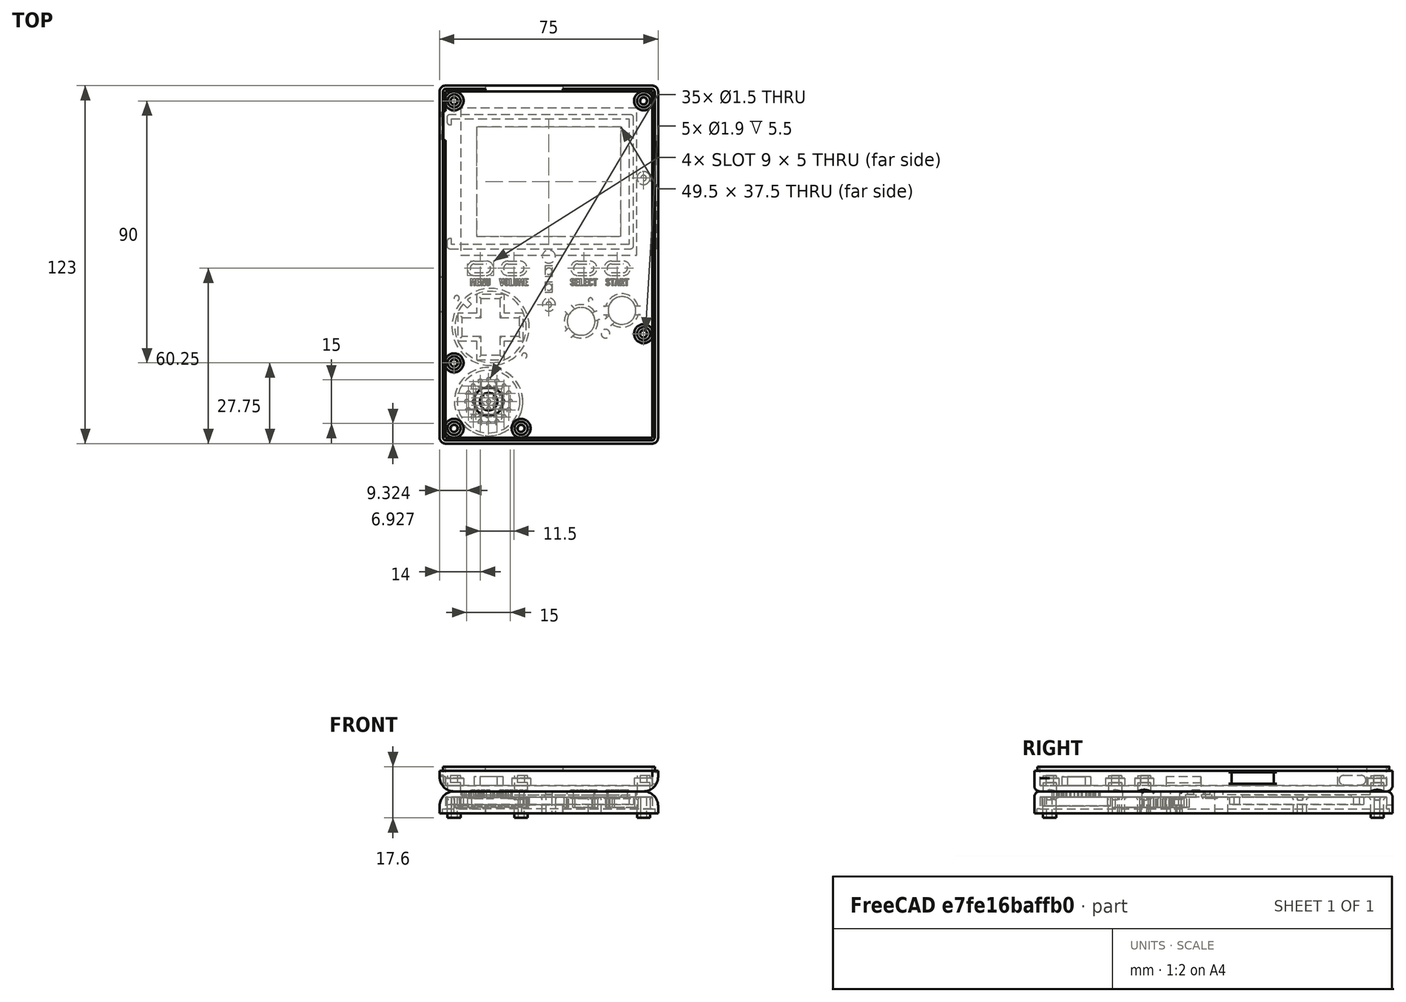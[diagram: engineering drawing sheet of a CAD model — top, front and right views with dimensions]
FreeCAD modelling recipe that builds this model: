
FCSTD DOCUMENT  (FreeCAD 1.0R39319 (Git))
Label: redroid_go
License: All rights reserved
LicenseURL: https://en.wikipedia.org/wiki/All_rights_reserved
objects: Sketcher::SketchObject×37, PartDesign::Pad×18, PartDesign::Pocket×15, PartDesign::Fillet×14, PartDesign::SubShapeBinder×6, Part::Part2DObjectPython×4, Part::Extrusion×4, PartDesign::PolarPattern×3, Measure::MeasureLength×3, PartDesign::Body×2, Spreadsheet::Sheet×1, Measure::MeasureDistance×1, App::DocumentObjectGroup×1
note: 237 computed .brp shape members not serialized (recipe doc carries the construction recipe); baked Part::Feature solids carry a one-line shape summary decoded from their .brp

FEATURE [Spreadsheet::Sheet] Spreadsheet
  cells = A1='thickness; B1=2; A2='front_height; B2=5.5; A3='pcb_height; B3=1.6; A4='back_height; B4=3.5; A5='edges_fillet; B5=2
FEATURE [Sketcher::SketchObject] Sketch021  label="skrews"
  ArcFitTolerance = 1e-06
  AttachmentOffset = pos=(0,0,-2) rot=(0,0,1;0rad)
  AttachmentSupport = -> [XY_Plane002]
  FullyConstrained = true
  MakeInternals = false
  MapMode = 5
  Placement = pos=(0,0,-2) rot=(0,0,1;0rad)
  sketch-geometry (21):
    g0: Circle CenterX=-32.525 CenterY=45 CenterZ=0 NormalX=0 NormalY=0 NormalZ=1 AngleXU=0 Radius=0.95
    g1: Circle CenterX=-32.525 CenterY=-45 CenterZ=0 NormalX=0 NormalY=0 NormalZ=1 AngleXU=0 Radius=0.95
    g2: Circle CenterX=32.525 CenterY=18.5 CenterZ=0 NormalX=0 NormalY=0 NormalZ=1 AngleXU=0 Radius=0.95
    g3: Circle CenterX=32.525 CenterY=-35 CenterZ=0 NormalX=0 NormalY=0 NormalZ=1 AngleXU=0 Radius=0.95
    g4: Circle CenterX=-32.525 CenterY=45 CenterZ=0 NormalX=0 NormalY=0 NormalZ=1 AngleXU=0 Radius=2.25
    g5: Circle CenterX=-32.525 CenterY=-45 CenterZ=0 NormalX=0 NormalY=0 NormalZ=1 AngleXU=0 Radius=2.25
    g6: Circle CenterX=32.525 CenterY=-35 CenterZ=0 NormalX=0 NormalY=0 NormalZ=1 AngleXU=0 Radius=2.25
    g7: Circle CenterX=32.525 CenterY=18.5 CenterZ=0 NormalX=0 NormalY=0 NormalZ=1 AngleXU=0 Radius=2.25
    g8: LineSegment [constr] StartX=-32.525 StartY=45 StartZ=0 EndX=-32.525 EndY=-45 EndZ=0
    g9: LineSegment [constr] StartX=32.525 StartY=18.5 StartZ=0 EndX=32.525 EndY=-35 EndZ=0
    g10: LineSegment [constr] StartX=-32.525 StartY=45 StartZ=0 EndX=-32.525 EndY=-45 EndZ=0
    g11: LineSegment [constr] StartX=-32.525 StartY=-45 StartZ=0 EndX=32.525 EndY=-45 EndZ=0
    g12: LineSegment [constr] StartX=32.525 StartY=-45 StartZ=0 EndX=32.525 EndY=45 EndZ=0
    g13: LineSegment [constr] StartX=32.525 StartY=45 StartZ=0 EndX=-32.525 EndY=45 EndZ=0
    g14: Circle CenterX=0 CenterY=-25 CenterZ=0 NormalX=0 NormalY=0 NormalZ=1 AngleXU=0 Radius=0.95
    g15: Circle CenterX=0 CenterY=-25 CenterZ=0 NormalX=0 NormalY=0 NormalZ=1 AngleXU=0 Radius=2.25
    g16: LineSegment [constr] StartX=0 StartY=-25 StartZ=0 EndX=-32.525 EndY=-25 EndZ=0
    g17: LineSegment [constr] StartX=-32.525 StartY=-25 StartZ=0 EndX=-32.525 EndY=-45 EndZ=0
    g18: LineSegment [constr] StartX=-32.525 StartY=-45 StartZ=0 EndX=0 EndY=-45 EndZ=0
    g19: LineSegment [constr] StartX=0 StartY=-45 StartZ=0 EndX=0 EndY=-25 EndZ=0
    g20: Circle CenterX=0 CenterY=-8.5 CenterZ=0 NormalX=0 NormalY=0 NormalZ=1 AngleXU=0 Radius=2.25
  constraints (51):
    c: Equal(g0,g1)
    c: Equal(g1,g3)
    c: Equal(g3,g2)
    c: Diameter(g0) = 1.9
    c: Coincident(g4,g0)
    c: Coincident(g5,g1)
    c: Coincident(g6,g3)
    c: Coincident(g7,g2)
    c: Diameter(g4) = 4.5
    c: Equal(g4,g5)
    c: Equal(g5,g6)
    c: Equal(g6,g7)
    c: Coincident(g8,g0)
    c: Coincident(g8,g1)
    c: Vertical(g8)
    c: Coincident(g9,g2)
    c: Coincident(g9,g3)
    c: Vertical(g9)
    c: DistanceX(g0,g2) = 65.05
    c: DistanceY(g2,g0) = 26.5
    c: DistanceY(g8,g8) = 90
    c: DistanceY(g9,g9) = 53.5
    c: Coincident(g10,g11)
    c: Coincident(g11,g12)
    c: Coincident(g12,g13)
    c: Coincident(g13,g10)
    c: Vertical(g12)
    c: Horizontal(g11)
    c: Horizontal(g13)
    c: Coincident(g10,g0)
    c: Coincident(g10,g1)
    c: Symmetric(g11,g0,g-1)
    c: PointOnObject(g3,g12)
    c: Equal(g1,g14)
    c: Equal(g5,g15)
    c: Coincident(g16,g17)
    c: Coincident(g17,g18)
    c: Coincident(g18,g19)
    c: Coincident(g19,g16)
    c: Horizontal(g16)
    c: Horizontal(g18)
    c: Vertical(g17)
    c: Vertical(g19)
    c: Coincident(g16,g14)
    c: Coincident(g17,g1)
    c: PointOnObject(g15,g-2)
    c: Coincident(g14,g15)
    c: DistanceY(g19,g19) = 20
    c: PointOnObject(g20,g-2)
    c: Equal(g15,g20)
    c: DistanceY(g14,g20) = 16.5
FEATURE [Sketcher::SketchObject] Sketch022  label="main"
  ArcFitTolerance = 1e-06
  AttachmentSupport = -> [XY_Plane002]
  ExternalGeometry = -> [Sketch021]
  FullyConstrained = true
  MakeInternals = false
  MapMode = 5
  expr: Constraints[171] = 111.27 - 2.54 / 2 - 103.5
  expr: Constraints[184] = 11.5 - 0.4
  expr: Constraints[281] = 7.5 + 0.165
  expr: Constraints[292] = 55 - 2.54 / 2
  expr: Constraints[299] = 105.77 - 2.54 / 2 - 103.5
  sketch-geometry (119):
    g0: LineSegment StartX=-35.5 StartY=48.25 StartZ=0 EndX=-35.5 EndY=-70.75 EndZ=0
    g1: LineSegment StartX=-35.5 StartY=-70.75 StartZ=0 EndX=35.5 EndY=-70.75 EndZ=0
    g2: LineSegment StartX=35.5 StartY=-70.75 StartZ=0 EndX=35.5 EndY=48.25 EndZ=0
    g3: LineSegment StartX=35.5 StartY=48.25 StartZ=0 EndX=-35.5 EndY=48.25 EndZ=0
    g4: Circle [constr] CenterX=-32.525 CenterY=45 CenterZ=0 NormalX=0 NormalY=0 NormalZ=1 AngleXU=0 Radius=2.25
    g5: LineSegment [constr] StartX=-32.525 StartY=45 StartZ=0 EndX=-32.525 EndY=47.25 EndZ=0
    g6: LineSegment [constr] StartX=-32.525 StartY=47.25 StartZ=0 EndX=-32.525 EndY=48.25 EndZ=0
    g7: LineSegment StartX=-24.75 StartY=36 StartZ=0 EndX=-24.75 EndY=-1.5 EndZ=0
    g8: LineSegment StartX=-24.75 StartY=-1.5 StartZ=0 EndX=24.75 EndY=-1.5 EndZ=0
    g9: LineSegment StartX=24.75 StartY=-1.5 StartZ=0 EndX=24.75 EndY=36 EndZ=0
    g10: LineSegment StartX=24.75 StartY=36 StartZ=0 EndX=-24.75 EndY=36 EndZ=0
    g11: LineSegment [constr] StartX=-32.525 StartY=45 StartZ=0 EndX=-32.525 EndY=36 EndZ=0
    g12: LineSegment [constr] StartX=-32.525 StartY=36 StartZ=0 EndX=-24.75 EndY=36 EndZ=0
    g13: LineSegment [constr] StartX=-24.75 StartY=36 StartZ=0 EndX=-24.75 EndY=45 EndZ=0
    g14: LineSegment [constr] StartX=-24.75 StartY=45 StartZ=0 EndX=-32.525 EndY=45 EndZ=0
    g15: LineSegment [constr] StartX=-24.75 StartY=36 StartZ=0 EndX=24.75 EndY=-1.5 EndZ=0
    g16: GeomPoint [constr] X=0 Y=17.25 Z=0
    g17: ArcOfCircle CenterX=21.5 CenterY=-12.5 CenterZ=0 NormalX=0 NormalY=0 NormalZ=1 AngleXU=0 Radius=1.5 StartAngle=1.5708 EndAngle=4.71239
    g18: ArcOfCircle CenterX=25.5 CenterY=-12.5 CenterZ=0 NormalX=0 NormalY=0 NormalZ=1 AngleXU=0 Radius=1.5 StartAngle=4.71239 EndAngle=7.85398
    g19: LineSegment StartX=21.5 StartY=-11 StartZ=0 EndX=25.5 EndY=-11 EndZ=0
    g20: LineSegment StartX=21.5 StartY=-14 StartZ=0 EndX=25.5 EndY=-14 EndZ=0
    g21: LineSegment [constr] StartX=21.5 StartY=-12.5 StartZ=0 EndX=20 EndY=-12.5 EndZ=0
    g22: LineSegment [constr] StartX=25.5 StartY=-12.5 StartZ=0 EndX=27 EndY=-12.5 EndZ=0
    g23: ArcOfCircle CenterX=10 CenterY=-12.5 CenterZ=0 NormalX=0 NormalY=0 NormalZ=1 AngleXU=0 Radius=1.5 StartAngle=1.5708 EndAngle=4.71239
    g24: ArcOfCircle CenterX=14 CenterY=-12.5 CenterZ=0 NormalX=0 NormalY=0 NormalZ=1 AngleXU=0 Radius=1.5 StartAngle=4.71239 EndAngle=7.85398
    g25: LineSegment StartX=10 StartY=-11 StartZ=0 EndX=14 EndY=-11 EndZ=0
    g26: LineSegment StartX=10 StartY=-14 StartZ=0 EndX=14 EndY=-14 EndZ=0
    g27: LineSegment [constr] StartX=10 StartY=-12.5 StartZ=0 EndX=8.5 EndY=-12.5 EndZ=0
    g28: LineSegment [constr] StartX=14 StartY=-12.5 StartZ=0 EndX=15.5 EndY=-12.5 EndZ=0
    g29: LineSegment [constr] StartX=10 StartY=-11 StartZ=0 EndX=14 EndY=-14 EndZ=0
    g30: LineSegment [constr] StartX=14 StartY=-11 StartZ=0 EndX=10 EndY=-14 EndZ=0
    g31: LineSegment [constr] StartX=21.5 StartY=-11 StartZ=0 EndX=25.5 EndY=-14 EndZ=0
    g32: LineSegment [constr] StartX=25.5 StartY=-11 StartZ=0 EndX=21.5 EndY=-14 EndZ=0
    g33: GeomPoint [constr] X=12 Y=-12.5 Z=0
    g34: GeomPoint [constr] X=23.5 Y=-12.5 Z=0
    g35: LineSegment [constr] StartX=12 StartY=-12.5 StartZ=0 EndX=23.5 EndY=-12.5 EndZ=0
    g36: ArcOfCircle CenterX=-14 CenterY=-12.5 CenterZ=0 NormalX=0 NormalY=0 NormalZ=1 AngleXU=0 Radius=1.5 StartAngle=1.5708 EndAngle=4.71239
    g37: ArcOfCircle CenterX=-10 CenterY=-12.5 CenterZ=0 NormalX=0 NormalY=0 NormalZ=1 AngleXU=0 Radius=1.5 StartAngle=4.71239 EndAngle=7.85398
    g38: LineSegment StartX=-14 StartY=-11 StartZ=0 EndX=-10 EndY=-11 EndZ=0
    g39: LineSegment StartX=-14 StartY=-14 StartZ=0 EndX=-10 EndY=-14 EndZ=0
    g40: LineSegment [constr] StartX=-14 StartY=-12.5 StartZ=0 EndX=-15.5 EndY=-12.5 EndZ=0
    g41: LineSegment [constr] StartX=-10 StartY=-12.5 StartZ=0 EndX=-8.5 EndY=-12.5 EndZ=0
    g42: ArcOfCircle CenterX=-25.5 CenterY=-12.5 CenterZ=0 NormalX=0 NormalY=0 NormalZ=1 AngleXU=0 Radius=1.5 StartAngle=1.5708 EndAngle=4.71239
    g43: ArcOfCircle CenterX=-21.5 CenterY=-12.5 CenterZ=0 NormalX=0 NormalY=0 NormalZ=1 AngleXU=0 Radius=1.5 StartAngle=4.71239 EndAngle=7.85398
    g44: LineSegment StartX=-25.5 StartY=-11 StartZ=0 EndX=-21.5 EndY=-11 EndZ=0
    g45: LineSegment StartX=-25.5 StartY=-14 StartZ=0 EndX=-21.5 EndY=-14 EndZ=0
    g46: LineSegment [constr] StartX=-25.5 StartY=-12.5 StartZ=0 EndX=-27 EndY=-12.5 EndZ=0
    g47: LineSegment [constr] StartX=-21.5 StartY=-12.5 StartZ=0 EndX=-20 EndY=-12.5 EndZ=0
    g48: LineSegment [constr] StartX=-25.5 StartY=-11 StartZ=0 EndX=-21.5 EndY=-14 EndZ=0
    g49: LineSegment [constr] StartX=-21.5 StartY=-11 StartZ=0 EndX=-25.5 EndY=-14 EndZ=0
    g50: LineSegment [constr] StartX=-14 StartY=-11 StartZ=0 EndX=-10 EndY=-14 EndZ=0
    g51: LineSegment [constr] StartX=-10 StartY=-11 StartZ=0 EndX=-14 EndY=-14 EndZ=0
    g52: GeomPoint [constr] X=-23.5 Y=-12.5 Z=0
    g53: GeomPoint [constr] X=-12 Y=-12.5 Z=0
    g54: LineSegment [constr] StartX=-23.5 StartY=-12.5 StartZ=0 EndX=-12 EndY=-12.5 EndZ=0
    g55: LineSegment [constr] StartX=-12 StartY=-12.5 StartZ=0 EndX=12 EndY=-12.5 EndZ=0
    g56: LineSegment [constr] StartX=-23.5 StartY=-12.5 StartZ=0 EndX=-23.5 EndY=-25 EndZ=0
    g57: LineSegment [constr] StartX=-23.5 StartY=-25 StartZ=0 EndX=0 EndY=-25 EndZ=0
    g58: LineSegment [constr] StartX=0 StartY=-25 StartZ=0 EndX=0 EndY=-12.5 EndZ=0
    g59: LineSegment [constr] StartX=0 StartY=-12.5 StartZ=0 EndX=-23.5 EndY=-12.5 EndZ=0
    g60: Circle CenterX=25.1094 CenterY=-27.01 CenterZ=0 NormalX=0 NormalY=0 NormalZ=1 AngleXU=0 Radius=4.75
    g61: Circle CenterX=11.1 CenterY=-30.75 CenterZ=0 NormalX=0 NormalY=0 NormalZ=1 AngleXU=0 Radius=4.75
    g62: LineSegment [constr] StartX=11.1 StartY=-30.75 StartZ=0 EndX=25.1094 EndY=-30.75 EndZ=0
    g63: LineSegment [constr] StartX=25.1094 StartY=-30.75 StartZ=0 EndX=25.1094 EndY=-27.01 EndZ=0
    g64: LineSegment [constr] StartX=25.1094 StartY=-27.01 StartZ=0 EndX=11.1 EndY=-27.01 EndZ=0
    g65: LineSegment [constr] StartX=11.1 StartY=-27.01 StartZ=0 EndX=11.1 EndY=-30.75 EndZ=0
    g66: Circle CenterX=0 CenterY=-19 CenterZ=0 NormalX=0 NormalY=0 NormalZ=1 AngleXU=0 Radius=1.1
    g67: LineSegment [constr] StartX=-10 StartY=-12.5 StartZ=0 EndX=-10 EndY=-19 EndZ=0
    g68: LineSegment [constr] StartX=-10 StartY=-19 StartZ=0 EndX=0 EndY=-19 EndZ=0
    g69: LineSegment [constr] StartX=0 StartY=-19 StartZ=0 EndX=0 EndY=-12.5 EndZ=0
    g70: LineSegment [constr] StartX=0 StartY=-12.5 StartZ=0 EndX=-10 EndY=-12.5 EndZ=0
    g71: LineSegment [constr] StartX=0 StartY=-25 StartZ=0 EndX=0 EndY=-30.75 EndZ=0
    g72: LineSegment [constr] StartX=0 StartY=-30.75 StartZ=0 EndX=11.1 EndY=-30.75 EndZ=0
    g73: LineSegment [constr] StartX=11.1 StartY=-30.75 StartZ=0 EndX=11.1 EndY=-25 EndZ=0
    g74: LineSegment [constr] StartX=11.1 StartY=-25 StartZ=0 EndX=0 EndY=-25 EndZ=0
    g75: LineSegment StartX=-23.25 StartY=-29.415 StartZ=0 EndX=-23.25 EndY=-22.915 EndZ=0
    g76: LineSegment StartX=-23.25 StartY=-22.915 StartZ=0 EndX=-16.75 EndY=-22.915 EndZ=0
    g77: LineSegment StartX=-16.75 StartY=-22.915 StartZ=0 EndX=-16.75 EndY=-29.415 EndZ=0
    g78: LineSegment StartX=-16.75 StartY=-29.415 StartZ=0 EndX=-10.25 EndY=-29.415 EndZ=0
    g79: LineSegment StartX=-10.25 StartY=-29.415 StartZ=0 EndX=-10.25 EndY=-35.915 EndZ=0
    g80: LineSegment StartX=-10.25 StartY=-35.915 StartZ=0 EndX=-16.75 EndY=-35.915 EndZ=0
    g81: LineSegment StartX=-16.75 StartY=-35.915 StartZ=0 EndX=-16.75 EndY=-42.415 EndZ=0
    g82: LineSegment StartX=-16.75 StartY=-42.415 StartZ=0 EndX=-23.25 EndY=-42.415 EndZ=0
    g83: LineSegment StartX=-23.25 StartY=-42.415 StartZ=0 EndX=-23.25 EndY=-35.915 EndZ=0
    g84: LineSegment StartX=-23.25 StartY=-35.915 StartZ=0 EndX=-29.75 EndY=-35.915 EndZ=0
    g85: LineSegment StartX=-29.75 StartY=-35.915 StartZ=0 EndX=-29.75 EndY=-29.415 EndZ=0
    g86: LineSegment StartX=-29.75 StartY=-29.415 StartZ=0 EndX=-23.25 EndY=-29.415 EndZ=0
    g87: LineSegment [constr] StartX=-29.75 StartY=-29.415 StartZ=0 EndX=-23.25 EndY=-29.415 EndZ=0
    g88: LineSegment [constr] StartX=-23.25 StartY=-29.415 StartZ=0 EndX=-23.25 EndY=-22.915 EndZ=0
    g89: LineSegment [constr] StartX=-23.25 StartY=-22.915 StartZ=0 EndX=-29.75 EndY=-22.915 EndZ=0
    g90: LineSegment [constr] StartX=-29.75 StartY=-22.915 StartZ=0 EndX=-29.75 EndY=-29.415 EndZ=0
    g91: LineSegment [constr] StartX=-29.75 StartY=-35.915 StartZ=0 EndX=-29.75 EndY=-42.415 EndZ=0
    g92: LineSegment [constr] StartX=-29.75 StartY=-42.415 StartZ=0 EndX=-23.25 EndY=-42.415 EndZ=0
    g93: LineSegment [constr] StartX=-23.25 StartY=-42.415 StartZ=0 EndX=-23.25 EndY=-35.915 EndZ=0
    g94: LineSegment [constr] StartX=-23.25 StartY=-35.915 StartZ=0 EndX=-29.75 EndY=-35.915 EndZ=0
    g95: LineSegment [constr] StartX=-16.75 StartY=-42.415 StartZ=0 EndX=-10.25 EndY=-42.415 EndZ=0
    g96: LineSegment [constr] StartX=-10.25 StartY=-42.415 StartZ=0 EndX=-10.25 EndY=-35.915 EndZ=0
    g97: LineSegment [constr] StartX=-10.25 StartY=-35.915 StartZ=0 EndX=-16.75 EndY=-35.915 EndZ=0
    g98: LineSegment [constr] StartX=-16.75 StartY=-35.915 StartZ=0 EndX=-16.75 EndY=-42.415 EndZ=0
    g99: LineSegment [constr] StartX=-10.25 StartY=-29.415 StartZ=0 EndX=-10.25 EndY=-22.915 EndZ=0
    g100: LineSegment [constr] StartX=-10.25 StartY=-22.915 StartZ=0 EndX=-16.75 EndY=-22.915 EndZ=0
    g101: LineSegment [constr] StartX=-16.75 StartY=-22.915 StartZ=0 EndX=-16.75 EndY=-29.415 EndZ=0
    g102: LineSegment [constr] StartX=-16.75 StartY=-29.415 StartZ=0 EndX=-10.25 EndY=-29.415 EndZ=0
    g103: LineSegment [constr] StartX=-23.25 StartY=-29.415 StartZ=0 EndX=-23.25 EndY=-35.915 EndZ=0
    g104: LineSegment [constr] StartX=-23.25 StartY=-35.915 StartZ=0 EndX=-16.75 EndY=-35.915 EndZ=0
    g105: LineSegment [constr] StartX=-16.75 StartY=-35.915 StartZ=0 EndX=-16.75 EndY=-29.415 EndZ=0
    g106: LineSegment [constr] StartX=-16.75 StartY=-29.415 StartZ=0 EndX=-23.25 EndY=-29.415 EndZ=0
    g107: LineSegment [constr] StartX=-23.25 StartY=-29.415 StartZ=0 EndX=-16.75 EndY=-35.915 EndZ=0
    g108: LineSegment [constr] StartX=-23.25 StartY=-35.915 StartZ=0 EndX=-16.75 EndY=-29.415 EndZ=0
    g109: GeomPoint [constr] X=-20 Y=-32.665 Z=0
    g110: LineSegment [constr] StartX=-20 StartY=-32.665 StartZ=0 EndX=0 EndY=-32.665 EndZ=0
    g111: LineSegment [constr] StartX=0 StartY=-32.665 StartZ=0 EndX=0 EndY=-25 EndZ=0
    g112: LineSegment [constr] StartX=0 StartY=-25 StartZ=0 EndX=-20 EndY=-25 EndZ=0
    g113: LineSegment [constr] StartX=-20 StartY=-25 StartZ=0 EndX=-20 EndY=-32.665 EndZ=0
    g114: LineSegment [constr] StartX=-32.525 StartY=45 StartZ=0 EndX=-32.525 EndY=-8.73 EndZ=0
    g115: LineSegment [constr] StartX=-32.525 StartY=-8.73 StartZ=0 EndX=-32.025 EndY=-8.73 EndZ=0
    g116: LineSegment [constr] StartX=-32.025 StartY=-8.73 StartZ=0 EndX=-32.025 EndY=45 EndZ=0
    g117: LineSegment [constr] StartX=-32.025 StartY=45 StartZ=0 EndX=-32.525 EndY=45 EndZ=0
    g118: Circle CenterX=0 CenterY=-13.5 CenterZ=0 NormalX=0 NormalY=0 NormalZ=1 AngleXU=0 Radius=1.1
  constraints (300):
    c: Coincident(g0,g1)
    c: Coincident(g1,g2)
    c: Coincident(g2,g3)
    c: Coincident(g3,g0)
    c: Vertical(g0)
    c: Vertical(g2)
    c: Horizontal(g1)
    c: DistanceX(g3,g3) = 71
    c: Symmetric(g0,g2,g-2)
    c: DistanceY(g2,g2) = 119
    c: Coincident(g4,g-3)
    c: Equal(g4,g-3)
    c: Coincident(g5,g4)
    c: PointOnObject(g5,g4)
    c: Vertical(g5)
    c: Coincident(g6,g5)
    c: PointOnObject(g6,g3)
    c: Vertical(g6)
    c: DistanceY(g6,g6) = 1
    c: Coincident(g7,g8)
    c: Coincident(g8,g9)
    c: Coincident(g9,g10)
    c: Coincident(g10,g7)
    c: Vertical(g7)
    c: Vertical(g9)
    c: Horizontal(g8)
    c: DistanceX(g10,g10) = 49.5
    c: DistanceY(g9,g9) = 37.5
    c: Symmetric(g7,g9,g-2)
    c: Coincident(g11,g12)
    c: Coincident(g12,g13)
    c: Coincident(g13,g14)
    c: Coincident(g14,g11)
    c: Vertical(g11)
    c: Vertical(g13)
    c: Horizontal(g12)
    c: Horizontal(g14)
    c: Coincident(g11,g4)
    c: Coincident(g12,g7)
    c: DistanceY(g13,g13) = 9
    c: Coincident(g15,g7)
    c: Coincident(g15,g8)
    c: PointOnObject(g16,g15)
    c: PointOnObject(g16,g-2)
    c: Tangent(g17,g19) = 1.5708
    c: Tangent(g17,g20) = -1.5708
    c: Tangent(g18,g19) = 1.5708
    c: Tangent(g18,g20) = -1.5708
    c: Equal(g17,g18)
    c: Horizontal(g19)
    c: DistanceY(g17,g17) = 3
    c: Coincident(g21,g17)
    c: PointOnObject(g21,g17)
    c: Horizontal(g21)
    c: Coincident(g22,g18)
    c: PointOnObject(g22,g18)
    c: Horizontal(g22)
    c: DistanceX(g21,g22) = 7
    c: Tangent(g23,g25) = 1.5708
    c: Tangent(g23,g26) = -1.5708
    c: Tangent(g24,g25) = 1.5708
    c: Tangent(g24,g26) = -1.5708
    c: Equal(g23,g24)
    c: Horizontal(g25)
    c: DistanceY(g23,g23) = 3
    c: Coincident(g27,g23)
    c: PointOnObject(g27,g23)
    c: Horizontal(g27)
    c: Coincident(g28,g24)
    c: PointOnObject(g28,g24)
    c: Horizontal(g28)
    c: DistanceX(g27,g28) = 7
    c: Coincident(g29,g23)
    c: Coincident(g29,g24)
    c: Coincident(g30,g24)
    c: Coincident(g30,g23)
    c: Coincident(g31,g17)
    c: Coincident(g31,g18)
    c: Coincident(g32,g18)
    c: Coincident(g32,g17)
    c: PointOnObject(g33,g29)
    c: PointOnObject(g34,g31)
    c: PointOnObject(g33,g30)
    c: PointOnObject(g34,g32)
    c: Coincident(g35,g33)
    c: Coincident(g35,g34)
    c: Horizontal(g35)
    c: DistanceX(g35,g35) = 11.5
    c: Tangent(g36,g38) = 1.5708
    c: Tangent(g36,g39) = -1.5708
    c: Tangent(g37,g38) = 1.5708
    c: Tangent(g37,g39) = -1.5708
    c: Equal(g36,g37)
    c: Horizontal(g38)
    c: DistanceY(g36,g36) = 3
    c: Coincident(g40,g36)
    c: PointOnObject(g40,g36)
    c: Horizontal(g40)
    c: Coincident(g41,g37)
    c: PointOnObject(g41,g37)
    c: Horizontal(g41)
    c: DistanceX(g40,g41) = 7
    c: Tangent(g42,g44) = 1.5708
    c: Tangent(g42,g45) = -1.5708
    c: Tangent(g43,g44) = 1.5708
    c: Tangent(g43,g45) = -1.5708
    c: Equal(g42,g43)
    c: Horizontal(g44)
    c: DistanceY(g42,g42) = 3
    c: Coincident(g46,g42)
    c: PointOnObject(g46,g42)
    c: Horizontal(g46)
    c: Coincident(g47,g43)
    c: PointOnObject(g47,g43)
    c: Horizontal(g47)
    c: DistanceX(g46,g47) = 7
    c: Coincident(g48,g42)
    c: Coincident(g48,g43)
    c: Coincident(g49,g43)
    c: Coincident(g49,g42)
    c: Coincident(g50,g36)
    c: Coincident(g50,g37)
    c: Coincident(g51,g37)
    c: Coincident(g51,g36)
    c: PointOnObject(g52,g48)
    c: PointOnObject(g53,g50)
    c: PointOnObject(g52,g49)
    c: PointOnObject(g53,g51)
    c: Coincident(g54,g52)
    c: Coincident(g54,g53)
    c: Horizontal(g54)
    c: DistanceX(g54,g54) = 11.5
    c: DistanceX(g55,g55) = 24
    c: Coincident(g55,g53)
    c: Coincident(g55,g33)
    c: Symmetric(g52,g34,g-2)
    c: Coincident(g56,g57)
    c: Coincident(g57,g58)
    c: Coincident(g58,g59)
    c: Coincident(g59,g56)
    c: Vertical(g56)
    c: Vertical(g58)
    c: Horizontal(g57)
    c: Horizontal(g59)
    c: Coincident(g56,g52)
    c: Coincident(g57,g-4)
    c: DistanceY(g56,g56) = 12.5
    c: Diameter(g60) = 9.5
    c: Equal(g60,g61)
    c: Coincident(g62,g63)
    c: Coincident(g63,g64)
    c: Coincident(g64,g65)
    c: Coincident(g65,g62)
    c: Horizontal(g62)
    c: Horizontal(g64)
    c: Vertical(g63)
    c: Vertical(g65)
    c: Coincident(g62,g61)
    c: Coincident(g63,g60)
    c: PointOnObject(g66,g58)
    c: Diameter(g66) = 2.2
    c: Coincident(g67,g68)
    c: Coincident(g68,g69)
    c: Coincident(g69,g70)
    c: Coincident(g70,g67)
    c: Vertical(g67)
    c: Vertical(g69)
    c: Horizontal(g68)
    c: Horizontal(g70)
    c: Coincident(g67,g37)
    c: Coincident(g68,g66)
    c: DistanceY(g67,g67) = 6.5
    c: DistanceY(g63,g63) = 3.74
    c: Distance(g61,g60) = 14.5
    c: Coincident(g71,g72)
    c: Coincident(g72,g73)
    c: Coincident(g73,g74)
    c: Coincident(g74,g71)
    c: Vertical(g71)
    c: Vertical(g73)
    c: Horizontal(g72)
    c: Horizontal(g74)
    c: Coincident(g71,g57)
    c: Coincident(g72,g61)
    c: DistanceX(g74,g74) = 11.1
    c: DistanceY(g73,g73) = 5.75
    c: Vertical(g75)
    c: Coincident(g75,g76)
    c: Horizontal(g76)
    c: Coincident(g76,g77)
    c: Coincident(g77,g78)
    c: Horizontal(g78)
    c: Coincident(g78,g79)
    c: Vertical(g79)
    c: Coincident(g79,g80)
    c: Coincident(g80,g81)
    c: Vertical(g81)
    c: Coincident(g81,g82)
    c: Coincident(g82,g83)
    c: Vertical(g83)
    c: Coincident(g83,g84)
    c: Coincident(g84,g85)
    c: Coincident(g85,g86)
    c: Coincident(g86,g75)
    c: Horizontal(g86)
    c: Horizontal(g82)
    c: Horizontal(g84)
    c: Horizontal(g80)
    c: Vertical(g85)
    c: Vertical(g77)
    c: Coincident(g87,g88)
    c: Coincident(g88,g89)
    c: Coincident(g89,g90)
    c: Coincident(g90,g87)
    c: Horizontal(g87)
    c: Horizontal(g89)
    c: Vertical(g88)
    c: Vertical(g90)
    c: Coincident(g87,g85)
    c: Coincident(g88,g75)
    c: Coincident(g91,g92)
    c: Coincident(g92,g93)
    c: Coincident(g93,g94)
    c: Coincident(g94,g91)
    c: Vertical(g91)
    c: Vertical(g93)
    c: Horizontal(g92)
    c: Horizontal(g94)
    c: Coincident(g91,g84)
    c: Coincident(g92,g82)
    c: Coincident(g95,g96)
    c: Coincident(g96,g97)
    c: Coincident(g97,g98)
    c: Coincident(g98,g95)
    c: Horizontal(g95)
    c: Horizontal(g97)
    c: Vertical(g96)
    c: Vertical(g98)
    c: Coincident(g95,g81)
    c: Coincident(g96,g79)
    c: Coincident(g99,g100)
    c: Coincident(g100,g101)
    c: Coincident(g101,g102)
    c: Coincident(g102,g99)
    c: Vertical(g99)
    c: Vertical(g101)
    c: Horizontal(g100)
    c: Horizontal(g102)
    c: Coincident(g99,g78)
    c: Coincident(g100,g76)
    c: Coincident(g103,g104)
    c: Coincident(g104,g105)
    c: Coincident(g105,g106)
    c: Coincident(g106,g103)
    c: Vertical(g103)
    c: Vertical(g105)
    c: Horizontal(g104)
    c: Horizontal(g106)
    c: Coincident(g103,g75)
    c: Coincident(g104,g80)
    c: Equal(g106,g105)
    c: Coincident(g77,g105)
    c: Coincident(g83,g103)
    c: DistanceX(g76,g76) = 6.5
    c: Coincident(g107,g75)
    c: Coincident(g107,g80)
    c: Coincident(g108,g83)
    c: Coincident(g108,g77)
    c: PointOnObject(g109,g107)
    c: PointOnObject(g109,g108)
    c: Coincident(g110,g111)
    c: Coincident(g111,g112)
    c: Coincident(g112,g113)
    c: Coincident(g113,g110)
    c: Horizontal(g110)
    c: Horizontal(g112)
    c: Vertical(g111)
    c: Vertical(g113)
    c: Coincident(g110,g109)
    c: Coincident(g111,g57)
    c: DistanceX(g110,g110) = 20
    c: DistanceY(g113,g113) = 7.665
    c: Coincident(g114,g115)
    c: Coincident(g115,g116)
    c: Coincident(g116,g117)
    c: Coincident(g117,g114)
    c: Vertical(g114)
    c: Vertical(g116)
    c: Horizontal(g115)
    c: Horizontal(g117)
    c: Coincident(g114,g4)
    c: DistanceX(g115,g115) = 0.5
    c: DistanceY(g114,g114) = 53.73
    c: DistanceX(g89,g99) = 19.5
    c: Equal(g89,g90)
    c: Equal(g89,g100)
    c: Equal(g96,g99)
    c: PointOnObject(g118,g58)
    c: Equal(g66,g118)
    c: DistanceY(g118,g37) = 1
FEATURE [Sketcher::SketchObject] Sketch023  label="border"
  ArcFitTolerance = 1e-06
  AttachmentSupport = -> [XY_Plane002]
  ExternalGeometry = -> [Sketch022]
  FullyConstrained = true
  MakeInternals = false
  MapMode = 5
  expr: Constraints[31] = Spreadsheet.B1
  sketch-geometry (16):
    g0: LineSegment StartX=-37.5 StartY=50.25 StartZ=0 EndX=-37.5 EndY=-72.75 EndZ=0
    g1: LineSegment StartX=-37.5 StartY=-72.75 StartZ=0 EndX=37.5 EndY=-72.75 EndZ=0
    g2: LineSegment StartX=37.5 StartY=-72.75 StartZ=0 EndX=37.5 EndY=50.25 EndZ=0
    g3: LineSegment StartX=37.5 StartY=50.25 StartZ=0 EndX=-37.5 EndY=50.25 EndZ=0
    g4: LineSegment [constr] StartX=-37.5 StartY=50.25 StartZ=0 EndX=-37.5 EndY=48.25 EndZ=0
    g5: LineSegment [constr] StartX=-37.5 StartY=48.25 StartZ=0 EndX=-35.5 EndY=48.25 EndZ=0
    g6: LineSegment [constr] StartX=-35.5 StartY=48.25 StartZ=0 EndX=-35.5 EndY=50.25 EndZ=0
    g7: LineSegment [constr] StartX=-35.5 StartY=50.25 StartZ=0 EndX=-37.5 EndY=50.25 EndZ=0
    g8: LineSegment [constr] StartX=35.5 StartY=-70.75 StartZ=0 EndX=35.5 EndY=-72.75 EndZ=0
    g9: LineSegment [constr] StartX=35.5 StartY=-72.75 StartZ=0 EndX=37.5 EndY=-72.75 EndZ=0
    g10: LineSegment [constr] StartX=37.5 StartY=-72.75 StartZ=0 EndX=37.5 EndY=-70.75 EndZ=0
    g11: LineSegment [constr] StartX=37.5 StartY=-70.75 StartZ=0 EndX=35.5 EndY=-70.75 EndZ=0
    g12: LineSegment StartX=-35.5 StartY=48.25 StartZ=0 EndX=-35.5 EndY=-70.75 EndZ=0
    g13: LineSegment StartX=-35.5 StartY=-70.75 StartZ=0 EndX=35.5 EndY=-70.75 EndZ=0
    g14: LineSegment StartX=35.5 StartY=-70.75 StartZ=0 EndX=35.5 EndY=48.25 EndZ=0
    g15: LineSegment StartX=35.5 StartY=48.25 StartZ=0 EndX=-35.5 EndY=48.25 EndZ=0
  constraints (42):
    c: Coincident(g0,g1)
    c: Coincident(g1,g2)
    c: Coincident(g2,g3)
    c: Coincident(g3,g0)
    c: Vertical(g0)
    c: Vertical(g2)
    c: Horizontal(g1)
    c: Horizontal(g3)
    c: Coincident(g4,g5)
    c: Coincident(g5,g6)
    c: Coincident(g6,g7)
    c: Coincident(g7,g4)
    c: Vertical(g4)
    c: Vertical(g6)
    c: Horizontal(g5)
    c: Horizontal(g7)
    c: Coincident(g4,g0)
    c: Coincident(g5,g-3)
    c: Coincident(g8,g9)
    c: Coincident(g9,g10)
    c: Coincident(g10,g11)
    c: Coincident(g11,g8)
    c: Vertical(g8)
    c: Vertical(g10)
    c: Horizontal(g9)
    c: Horizontal(g11)
    c: Coincident(g8,g-4)
    c: Coincident(g9,g1)
    c: Equal(g5,g6)
    c: Equal(g6,g11)
    c: Equal(g11,g8)
    c: DistanceX(g5,g5) = 2
    c: Coincident(g12,g13)
    c: Coincident(g13,g14)
    c: Coincident(g14,g15)
    c: Coincident(g15,g12)
    c: Vertical(g12)
    c: Vertical(g14)
    c: Horizontal(g13)
    c: Horizontal(g15)
    c: Coincident(g12,g5)
    c: Coincident(g13,g8)
FEATURE [PartDesign::Pad] Pad011
  Direction = (0,0,1)
  Length = 7.5
  Length2 = 10
  Profile = -> Sketch023
  ReferenceAxis = -> Sketch023 [N_Axis]
  Refine = true
  Reversed = true
  Suppressed = false
  Type = 0
  expr: Length = Spreadsheet.B1 + Spreadsheet.B2
FEATURE [PartDesign::Pad] Pad012
  BaseFeature = -> Pad011
  Direction = (0,0,1)
  Length = 2
  Length2 = 10
  Profile = -> Sketch022
  ReferenceAxis = -> Sketch022 [N_Axis]
  Refine = true
  Reversed = true
  Suppressed = false
  Type = 0
  expr: Length = Spreadsheet.B1
FEATURE [PartDesign::Fillet] Fillet004
  Base = -> Pad012 [Edge16,Edge3]
  BaseFeature = -> Pad012
  Radius = 5
  Refine = true
  SupportTransform = false
  Suppressed = false
  UseAllEdges = false
FEATURE [PartDesign::Pad] Pad013
  BaseFeature = -> Fillet004
  Direction = (0,0,1)
  Length = 5.5
  Length2 = 10
  Profile = -> Sketch021
  ReferenceAxis = -> Sketch021 [N_Axis]
  Refine = true
  Reversed = true
  Suppressed = false
  Type = 0
  expr: Length = Spreadsheet.B2
FEATURE [PartDesign::Fillet] Fillet005
  Base = -> Pad013 [Edge19,Edge5]
  BaseFeature = -> Pad013
  Radius = 2
  Refine = true
  SupportTransform = false
  Suppressed = false
  UseAllEdges = false
  expr: Radius = Spreadsheet.B5
FEATURE [Sketcher::SketchObject] Sketch024  label="screen_lens_socket"
  ArcFitTolerance = 1e-06
  AttachmentSupport = -> [XY_Plane002]
  ExternalGeometry = -> [Sketch022]
  FullyConstrained = true
  MakeInternals = false
  MapMode = 5
  sketch-geometry (10):
    g0: LineSegment [constr] StartX=-24.75 StartY=36 StartZ=0 EndX=24.75 EndY=-1.5 EndZ=0
    g1: LineSegment [constr] StartX=24.75 StartY=36 StartZ=0 EndX=-24.75 EndY=-1.5 EndZ=0
    g2: GeomPoint [constr] X=-7e-16 Y=17.25 Z=0
    g3: LineSegment StartX=-30.25 StartY=42.5 StartZ=0 EndX=-30.25 EndY=-8 EndZ=0
    g4: LineSegment StartX=-30.25 StartY=-8 StartZ=0 EndX=30.25 EndY=-8 EndZ=0
    g5: LineSegment StartX=30.25 StartY=-8 StartZ=0 EndX=30.25 EndY=42.5 EndZ=0
    g6: LineSegment StartX=30.25 StartY=42.5 StartZ=0 EndX=-30.25 EndY=42.5 EndZ=0
    g7: LineSegment [constr] StartX=-30.25 StartY=42.5 StartZ=0 EndX=30.25 EndY=-8 EndZ=0
    g8: LineSegment [constr] StartX=30.25 StartY=42.5 StartZ=0 EndX=-30.25 EndY=-8 EndZ=0
    g9: GeomPoint [constr] X=-7e-16 Y=17.25 Z=0
  constraints (23):
    c: Coincident(g0,g-3)
    c: Coincident(g0,g-4)
    c: Coincident(g1,g-4)
    c: Coincident(g1,g-3)
    c: PointOnObject(g2,g0)
    c: PointOnObject(g2,g1)
    c: Coincident(g3,g4)
    c: Coincident(g4,g5)
    c: Coincident(g5,g6)
    c: Coincident(g6,g3)
    c: Vertical(g3)
    c: Vertical(g5)
    c: Horizontal(g4)
    c: Horizontal(g6)
    c: DistanceX(g6,g6) = 60.5
    c: DistanceY(g5,g5) = 50.5
    c: Coincident(g7,g3)
    c: Coincident(g7,g4)
    c: Coincident(g8,g5)
    c: Coincident(g8,g3)
    c: PointOnObject(g9,g7)
    c: PointOnObject(g9,g8)
    c: Coincident(g9,g2)
FEATURE [PartDesign::Pocket] Pocket008
  BaseFeature = -> Fillet005
  Direction = (0,0,-1)
  Length = 1.2
  Length2 = 5
  Profile = -> Sketch024
  ReferenceAxis = -> Sketch024 [N_Axis]
  Refine = true
  Suppressed = false
  Type = 0
FEATURE [Sketcher::SketchObject] Sketch025  label="menu_socket"
  ArcFitTolerance = 1e-06
  AttachmentOffset = pos=(0,0,-2) rot=(0,0,1;0rad)
  AttachmentSupport = -> [XY_Plane002]
  ExternalGeometry = -> [Sketch022]
  FullyConstrained = true
  MakeInternals = false
  MapMode = 5
  Placement = pos=(0,0,-2) rot=(0,0,1;0rad)
  expr: .AttachmentOffset.Base.z = -Spreadsheet.B1
  sketch-geometry (32):
    g0: ArcOfCircle CenterX=-14 CenterY=-12.5 CenterZ=0 NormalX=0 NormalY=0 NormalZ=1 AngleXU=0 Radius=1.5 StartAngle=1.5708 EndAngle=4.71239
    g1: ArcOfCircle CenterX=-10 CenterY=-12.5 CenterZ=0 NormalX=0 NormalY=0 NormalZ=1 AngleXU=0 Radius=1.5 StartAngle=4.71239 EndAngle=7.85398
    g2: LineSegment StartX=-14 StartY=-11 StartZ=0 EndX=-10 EndY=-11 EndZ=0
    g3: LineSegment StartX=-14 StartY=-14 StartZ=0 EndX=-10 EndY=-14 EndZ=0
    g4: ArcOfCircle CenterX=10 CenterY=-12.5 CenterZ=0 NormalX=0 NormalY=0 NormalZ=1 AngleXU=0 Radius=1.5 StartAngle=1.5708 EndAngle=4.71239
    g5: ArcOfCircle CenterX=14 CenterY=-12.5 CenterZ=0 NormalX=0 NormalY=0 NormalZ=1 AngleXU=0 Radius=1.5 StartAngle=4.71239 EndAngle=7.85398
    g6: LineSegment StartX=10 StartY=-11 StartZ=0 EndX=14 EndY=-11 EndZ=0
    g7: LineSegment StartX=10 StartY=-14 StartZ=0 EndX=14 EndY=-14 EndZ=0
    g8: ArcOfCircle CenterX=21.5 CenterY=-12.5 CenterZ=0 NormalX=0 NormalY=0 NormalZ=1 AngleXU=0 Radius=1.5 StartAngle=1.5708 EndAngle=4.71239
    g9: ArcOfCircle CenterX=25.5 CenterY=-12.5 CenterZ=0 NormalX=0 NormalY=0 NormalZ=1 AngleXU=0 Radius=1.5 StartAngle=4.71239 EndAngle=7.85398
    g10: LineSegment StartX=21.5 StartY=-11 StartZ=0 EndX=25.5 EndY=-11 EndZ=0
    g11: LineSegment StartX=21.5 StartY=-14 StartZ=0 EndX=25.5 EndY=-14 EndZ=0
    g12: ArcOfCircle CenterX=-25.5 CenterY=-12.5 CenterZ=0 NormalX=0 NormalY=0 NormalZ=1 AngleXU=0 Radius=2.5 StartAngle=1.5708 EndAngle=4.71239
    g13: ArcOfCircle CenterX=-21.5 CenterY=-12.5 CenterZ=0 NormalX=0 NormalY=0 NormalZ=1 AngleXU=0 Radius=2.5 StartAngle=4.71239 EndAngle=7.85398
    g14: LineSegment StartX=-25.5 StartY=-10 StartZ=0 EndX=-21.5 EndY=-10 EndZ=0
    g15: LineSegment StartX=-25.5 StartY=-15 StartZ=0 EndX=-21.5 EndY=-15 EndZ=0
    g16: ArcOfCircle CenterX=-14 CenterY=-12.5 CenterZ=0 NormalX=0 NormalY=0 NormalZ=1 AngleXU=0 Radius=2.5 StartAngle=1.5708 EndAngle=4.71239
    g17: ArcOfCircle CenterX=-10 CenterY=-12.5 CenterZ=0 NormalX=0 NormalY=0 NormalZ=1 AngleXU=0 Radius=2.5 StartAngle=4.71239 EndAngle=7.85398
    g18: LineSegment StartX=-14 StartY=-10 StartZ=0 EndX=-10 EndY=-10 EndZ=0
    g19: LineSegment StartX=-14 StartY=-15 StartZ=0 EndX=-10 EndY=-15 EndZ=0
    g20: ArcOfCircle CenterX=10 CenterY=-12.5 CenterZ=0 NormalX=0 NormalY=0 NormalZ=1 AngleXU=0 Radius=2.5 StartAngle=1.5708 EndAngle=4.71239
    g21: ArcOfCircle CenterX=14 CenterY=-12.5 CenterZ=0 NormalX=0 NormalY=0 NormalZ=1 AngleXU=0 Radius=2.5 StartAngle=4.71239 EndAngle=7.85398
    g22: LineSegment StartX=10 StartY=-10 StartZ=0 EndX=14 EndY=-10 EndZ=0
    g23: LineSegment StartX=10 StartY=-15 StartZ=0 EndX=14 EndY=-15 EndZ=0
    g24: ArcOfCircle CenterX=21.5 CenterY=-12.5 CenterZ=0 NormalX=0 NormalY=0 NormalZ=1 AngleXU=0 Radius=2.5 StartAngle=1.5708 EndAngle=4.71239
    g25: ArcOfCircle CenterX=25.5 CenterY=-12.5 CenterZ=0 NormalX=0 NormalY=0 NormalZ=1 AngleXU=0 Radius=2.5 StartAngle=4.71239 EndAngle=7.85398
    g26: LineSegment StartX=21.5 StartY=-10 StartZ=0 EndX=25.5 EndY=-10 EndZ=0
    g27: LineSegment StartX=21.5 StartY=-15 StartZ=0 EndX=25.5 EndY=-15 EndZ=0
    g28: ArcOfCircle CenterX=-25.5 CenterY=-12.5 CenterZ=0 NormalX=0 NormalY=0 NormalZ=1 AngleXU=0 Radius=1.5 StartAngle=1.5708 EndAngle=4.71239
    g29: ArcOfCircle CenterX=-21.5 CenterY=-12.5 CenterZ=0 NormalX=0 NormalY=0 NormalZ=1 AngleXU=0 Radius=1.5 StartAngle=4.71239 EndAngle=7.85398
    g30: LineSegment StartX=-25.5 StartY=-11 StartZ=0 EndX=-21.5 EndY=-11 EndZ=0
    g31: LineSegment StartX=-25.5 StartY=-14 StartZ=0 EndX=-21.5 EndY=-14 EndZ=0
  constraints (60):
    c: Tangent(g0,g2) = 1.5708
    c: Tangent(g0,g3) = -1.5708
    c: Tangent(g1,g2) = 1.5708
    c: Tangent(g1,g3) = -1.5708
    c: Tangent(g4,g6) = 1.5708
    c: Tangent(g4,g7) = -1.5708
    c: Tangent(g5,g6) = 1.5708
    c: Tangent(g5,g7) = -1.5708
    c: Tangent(g8,g10) = 1.5708
    c: Tangent(g8,g11) = -1.5708
    c: Tangent(g9,g10) = 1.5708
    c: Tangent(g9,g11) = -1.5708
    c: Tangent(g12,g14) = 1.5708
    c: Tangent(g12,g15) = -1.5708
    c: Tangent(g13,g14) = 1.5708
    c: Tangent(g13,g15) = -1.5708
    c: Equal(g12,g13)
    c: Tangent(g16,g18) = 1.5708
    c: Tangent(g16,g19) = -1.5708
    c: Tangent(g17,g18) = 1.5708
    c: Tangent(g17,g19) = -1.5708
    c: Equal(g16,g17)
    c: Tangent(g20,g22) = 1.5708
    c: Tangent(g20,g23) = -1.5708
    c: Tangent(g21,g22) = 1.5708
    c: Tangent(g21,g23) = -1.5708
    c: Equal(g20,g21)
    c: Tangent(g24,g26) = 1.5708
    c: Tangent(g24,g27) = -1.5708
    c: Tangent(g25,g26) = 1.5708
    c: Tangent(g25,g27) = -1.5708
    c: Equal(g24,g25)
    c: DistanceY(g-3,g13) = 1
    c: Coincident(g-4,g12)
    c: Coincident(g-3,g13)
    c: Equal(g13,g16)
    c: Equal(g13,g20)
    c: Equal(g13,g24)
    c: Coincident(g16,g0)
    c: Coincident(g0,g-5)
    c: Coincident(g0,g-5)
    c: Coincident(g1,g-6)
    c: Coincident(g17,g1)
    c: Coincident(g20,g4)
    c: Coincident(g4,g-7)
    c: Coincident(g4,g-7)
    c: Coincident(g5,g-8)
    c: Coincident(g21,g5)
    c: Coincident(g24,g8)
    c: Coincident(g9,g-10)
    c: Coincident(g-10,g9)
    c: Coincident(g25,g9)
    c: Coincident(g8,g-9)
    c: Tangent(g28,g30) = 1.5708
    c: Tangent(g28,g31) = -1.5708
    c: Tangent(g29,g30) = 1.5708
    c: Tangent(g29,g31) = -1.5708
    c: Coincident(g28,g12)
    c: Coincident(g29,g13)
    c: Coincident(g28,g-4)
FEATURE [PartDesign::Pad] Pad014
  BaseFeature = -> Pocket008
  Direction = (0,0,1)
  Length = 0.5
  Length2 = 10
  Profile = -> Sketch025
  ReferenceAxis = -> Sketch025 [N_Axis]
  Refine = true
  Reversed = true
  Suppressed = false
  Type = 0
FEATURE [Sketcher::SketchObject] Sketch026  label="ab_socket"
  ArcFitTolerance = 1e-06
  AttachmentOffset = pos=(0,0,-2) rot=(0,0,1;0rad)
  AttachmentSupport = -> [XY_Plane002]
  ExternalGeometry = -> [Sketch022]
  FullyConstrained = true
  MakeInternals = false
  MapMode = 5
  Placement = pos=(0,0,-2) rot=(0,0,1;0rad)
  expr: .AttachmentOffset.Base.z = -Spreadsheet.B1
  sketch-geometry (6):
    g0: Circle CenterX=11.1 CenterY=-30.75 CenterZ=0 NormalX=0 NormalY=0 NormalZ=1 AngleXU=0 Radius=4.75
    g1: Circle CenterX=25.1094 CenterY=-27.01 CenterZ=0 NormalX=0 NormalY=0 NormalZ=1 AngleXU=0 Radius=4.75
    g2: Circle CenterX=11.1 CenterY=-30.75 CenterZ=0 NormalX=0 NormalY=0 NormalZ=1 AngleXU=0 Radius=5.75
    g3: Circle CenterX=25.1094 CenterY=-27.01 CenterZ=0 NormalX=0 NormalY=0 NormalZ=1 AngleXU=0 Radius=5.75
    g4: LineSegment [constr] StartX=11.1 StartY=-30.75 StartZ=0 EndX=16.85 EndY=-30.75 EndZ=0
    g5: GeomPoint [constr] X=15.85 Y=-30.75 Z=0
  constraints (13):
    c: Coincident(g2,g0)
    c: Coincident(g3,g1)
    c: Equal(g2,g3)
    c: Coincident(g4,g0)
    c: PointOnObject(g4,g2)
    c: PointOnObject(g5,g4)
    c: PointOnObject(g5,g0)
    c: Distance(g5,g4) = 1
    c: Coincident(g0,g-3)
    c: Equal(g-3,g0)
    c: Equal(g1,g-4)
    c: Coincident(g1,g-4)
    c: Horizontal(g4)
FEATURE [PartDesign::Pad] Pad015
  BaseFeature = -> Pad014
  Direction = (0,0,1)
  Length = 3.5
  Length2 = 10
  Profile = -> Sketch026
  ReferenceAxis = -> Sketch026 [N_Axis]
  Refine = true
  Reversed = true
  Suppressed = false
  Type = 0
FEATURE [Sketcher::SketchObject] Sketch027  label="ab_socket_holes"
  ArcFitTolerance = 1e-06
  AttachmentOffset = pos=(0,0,-2) rot=(0,0,1;0rad)
  AttachmentSupport = -> [XY_Plane002]
  ExternalGeometry = -> [Sketch026]
  FullyConstrained = true
  MakeInternals = false
  MapMode = 5
  Placement = pos=(0,0,-2) rot=(0,0,1;0rad)
  expr: .AttachmentOffset.Base.z = -Spreadsheet.B1
  sketch-geometry (33):
    g0: LineSegment StartX=17.7609 StartY=-25.51 StartZ=0 EndX=17.7609 EndY=-28.51 EndZ=0
    g1: LineSegment StartX=17.7609 StartY=-28.51 StartZ=0 EndX=20.9882 EndY=-28.51 EndZ=0
    g2: LineSegment StartX=20.9882 StartY=-28.51 StartZ=0 EndX=18.5159 EndY=-30.5844 EndZ=0
    g3: LineSegment StartX=18.5159 StartY=-30.5844 StartZ=0 EndX=20.4443 EndY=-32.8826 EndZ=0
    g4: LineSegment StartX=20.4443 StartY=-32.8826 StartZ=0 EndX=25.6553 EndY=-28.51 EndZ=0
    g5: LineSegment StartX=25.6553 StartY=-28.51 StartZ=0 EndX=32.4578 EndY=-28.51 EndZ=0
    g6: LineSegment StartX=32.4578 StartY=-28.51 StartZ=0 EndX=32.4578 EndY=-25.51 EndZ=0
    g7: LineSegment StartX=32.4578 StartY=-25.51 StartZ=0 EndX=17.7609 EndY=-25.51 EndZ=0
    g8: LineSegment [constr] StartX=17.7609 StartY=-25.51 StartZ=0 EndX=32.4578 EndY=-28.51 EndZ=0
    g9: LineSegment [constr] StartX=17.7609 StartY=-28.51 StartZ=0 EndX=32.4578 EndY=-25.51 EndZ=0
    g10: GeomPoint [constr] X=25.1094 Y=-27.01 Z=0
    g11: Circle [constr] CenterX=25.1094 CenterY=-27.01 CenterZ=0 NormalX=0 NormalY=0 NormalZ=1 AngleXU=0 Radius=7.5
    g12: LineSegment [constr] StartX=25.1094 StartY=-27.01 StartZ=0 EndX=17.7609 EndY=-27.01 EndZ=0
    g13: LineSegment [constr] StartX=25.1094 StartY=-27.01 StartZ=0 EndX=19.4801 EndY=-31.7335 EndZ=0
    g14: LineSegment [constr] StartX=20.9882 StartY=-28.51 StartZ=0 EndX=23.3217 EndY=-28.51 EndZ=0
    g15: LineSegment [constr] StartX=25.6553 StartY=-28.51 StartZ=0 EndX=23.3217 EndY=-28.51 EndZ=0
    g16: Circle [constr] CenterX=11.1 CenterY=-30.75 CenterZ=0 NormalX=0 NormalY=0 NormalZ=1 AngleXU=0 Radius=7.5
    g17: LineSegment StartX=6.96451 StartY=-24.4932 StartZ=0 EndX=4.84319 EndY=-26.6145 EndZ=0
    g18: LineSegment StartX=4.84319 StartY=-26.6145 StartZ=0 EndX=8.97868 EndY=-30.75 EndZ=0
    g19: LineSegment StartX=8.97868 StartY=-30.75 StartZ=0 EndX=4.84319 EndY=-34.8855 EndZ=0
    g20: LineSegment StartX=4.84319 StartY=-34.8855 StartZ=0 EndX=6.96451 EndY=-37.0068 EndZ=0
    g21: LineSegment StartX=6.96451 StartY=-37.0068 StartZ=0 EndX=11.9255 EndY=-32.0458 EndZ=0
    g22: LineSegment StartX=11.9255 StartY=-32.0458 StartZ=0 EndX=18.5183 EndY=-29.6462 EndZ=0
    g23: LineSegment StartX=18.5183 StartY=-29.6462 StartZ=0 EndX=17.4923 EndY=-26.8271 EndZ=0
    g24: LineSegment StartX=17.4923 StartY=-26.8271 StartZ=0 EndX=11.4849 EndY=-29.0136 EndZ=0
    g25: LineSegment StartX=11.4849 StartY=-29.0136 StartZ=0 EndX=6.96451 EndY=-24.4932 EndZ=0
    g26: LineSegment [constr] StartX=6.96451 StartY=-24.4932 StartZ=0 EndX=11.1 EndY=-30.75 EndZ=0
    g27: LineSegment [constr] StartX=4.84319 StartY=-26.6145 StartZ=0 EndX=11.1 EndY=-30.75 EndZ=0
    g28: LineSegment [constr] StartX=11.1 StartY=-30.75 StartZ=0 EndX=4.84319 EndY=-34.8855 EndZ=0
    g29: LineSegment [constr] StartX=11.1 StartY=-30.75 StartZ=0 EndX=6.96451 EndY=-37.0068 EndZ=0
    g30: LineSegment [constr] StartX=11.1 StartY=-30.75 StartZ=0 EndX=17.4923 EndY=-26.8271 EndZ=0
    g31: LineSegment [constr] StartX=11.1 StartY=-30.75 StartZ=0 EndX=18.5183 EndY=-29.6462 EndZ=0
    g32: LineSegment [constr] StartX=11.1 StartY=-30.75 StartZ=0 EndX=3.6 EndY=-30.75 EndZ=0
  constraints (84):
    c: Coincident(g0,g1)
    c: Horizontal(g1)
    c: Coincident(g1,g2)
    c: Coincident(g2,g3)
    c: Coincident(g3,g4)
    c: Coincident(g4,g5)
    c: Horizontal(g5)
    c: Coincident(g5,g6)
    c: Coincident(g6,g7)
    c: Coincident(g7,g0)
    c: Horizontal(g7)
    c: Vertical(g0)
    c: Vertical(g6)
    c: Angle(g1,g2) = 0.698132
    c: Parallel(g2,g4)
    c: DistanceY(g0,g0) = 3
    c: Equal(g0,g3)
    c: Coincident(g8,g0)
    c: Coincident(g8,g5)
    c: Coincident(g9,g0)
    c: Coincident(g9,g6)
    c: Symmetric(g8,g8,g10)
    c: Coincident(g11,g10)
    c: PointOnObject(g2,g11)
    c: PointOnObject(g3,g11)
    c: PointOnObject(g0,g11)
    c: Symmetric(g0,g0,g12)
    c: Angle(g0,g12) = 1.5708
    c: Coincident(g13,g10)
    c: Symmetric(g3,g3,g13)
    c: Equal(g13,g12)
    c: Coincident(g14,g1)
    c: PointOnObject(g14,g13)
    c: Horizontal(g14)
    c: Coincident(g15,g4)
    c: Coincident(g15,g14)
    c: Horizontal(g15)
    c: Equal(g14,g15)
    c: Diameter(g11) = 15
    c: Equal(g16,g11)
    c: PointOnObject(g17,g16)
    c: PointOnObject(g17,g16)
    c: Coincident(g17,g18)
    c: Coincident(g18,g19)
    c: PointOnObject(g19,g16)
    c: Coincident(g19,g20)
    c: PointOnObject(g20,g16)
    c: Coincident(g20,g21)
    c: Coincident(g21,g22)
    c: PointOnObject(g22,g16)
    c: Coincident(g22,g23)
    c: PointOnObject(g23,g16)
    c: Coincident(g23,g24)
    c: Coincident(g24,g25)
    c: Coincident(g25,g17)
    c: Parallel(g18,g25)
    c: Parallel(g19,g21)
    c: Parallel(g22,g24)
    c: Equal(g17,g20)
    c: Equal(g20,g23)
    c: Equal(g17,g0)
    c: Angle(g18,g19) = 1.5708
    c: Angle(g24,g25) = 2.00713
    c: Angle(g18,g17) = 1.5708
    c: Angle(g20,g19) = 1.5708
    c: Angle(g23,g22) = 1.5708
    c: Coincident(g26,g17)
    c: Coincident(g26,g16)
    c: Coincident(g27,g17)
    c: Coincident(g27,g16)
    c: Coincident(g28,g16)
    c: Coincident(g28,g19)
    c: Coincident(g29,g16)
    c: Coincident(g29,g20)
    c: Coincident(g30,g16)
    c: Coincident(g30,g23)
    c: Coincident(g31,g16)
    c: Coincident(g31,g22)
    c: Coincident(g32,g16)
    c: PointOnObject(g32,g16)
    c: Horizontal(g32)
    c: PointOnObject(g18,g32)
    c: Coincident(g16,g-3)
    c: Coincident(g12,g-4)
FEATURE [Sketcher::SketchObject] Sketch028  label="dpad_socket001"
  ArcFitTolerance = 1e-06
  AttachmentOffset = pos=(0,0,-2) rot=(0,0,1;0rad)
  AttachmentSupport = -> [XY_Plane002]
  ExternalGeometry = -> [Sketch022]
  FullyConstrained = true
  MakeInternals = false
  MapMode = 5
  Placement = pos=(0,0,-2) rot=(0,0,1;0rad)
  expr: .AttachmentOffset.Base.z = -Spreadsheet.B1
  sketch-geometry (10):
    g0: LineSegment [constr] StartX=-23.25 StartY=-29.415 StartZ=0 EndX=-16.75 EndY=-35.915 EndZ=0
    g1: LineSegment [constr] StartX=-23.25 StartY=-35.915 StartZ=0 EndX=-16.75 EndY=-29.415 EndZ=0
    g2: GeomPoint [constr] X=-20 Y=-32.665 Z=0
    g3: ArcOfCircle CenterX=-20 CenterY=-32.665 CenterZ=0 NormalX=0 NormalY=0 NormalZ=1 AngleXU=0 Radius=12.25 StartAngle=2.43792 EndAngle=8.55766
    g4: Circle CenterX=-20 CenterY=-32.665 CenterZ=0 NormalX=0 NormalY=0 NormalZ=1 AngleXU=0 Radius=13.25
    g5: LineSegment StartX=-26.5118 StartY=-24.739 StartZ=0 EndX=-27.926 EndY=-23.3247 EndZ=0
    g6: LineSegment StartX=-29.3403 StartY=-24.739 StartZ=0 EndX=-27.926 EndY=-26.1532 EndZ=0
    g7: LineSegment StartX=-27.926 StartY=-26.1532 StartZ=0 EndX=-26.5118 EndY=-24.739 EndZ=0
    g8: Circle [constr] CenterX=-27.926 CenterY=-24.739 CenterZ=0 NormalX=0 NormalY=0 NormalZ=1 AngleXU=0 Radius=1.41421
    g9: LineSegment [constr] StartX=-27.926 StartY=-24.739 StartZ=0 EndX=-23.25 EndY=-29.415 EndZ=0
  constraints (25):
    c: Coincident(g0,g-7)
    c: Coincident(g0,g-10)
    c: Coincident(g1,g-9)
    c: Coincident(g1,g-8)
    c: PointOnObject(g2,g0)
    c: PointOnObject(g2,g1)
    c: Diameter(g3) = 24.5
    c: Coincident(g3,g2)
    c: Coincident(g4,g2)
    c: Diameter(g4) = 26.5
    c: Coincident(g6,g7)
    c: Coincident(g7,g5)
    c: Equal(g5,g6)
    c: Equal(g5,g7)
    c: PointOnObject(g5,g8)
    c: PointOnObject(g6,g8)
    c: PointOnObject(g6,g8)
    c: PointOnObject(g7,g8)
    c: Coincident(g3,g5)
    c: Coincident(g6,g3)
    c: Angle(g7,g6) = 1.5708
    c: Coincident(g9,g8)
    c: Coincident(g9,g0)
    c: Angle(g9,g-3) = 0.785398
    c: Distance(g7,g7) = 2
FEATURE [PartDesign::Pad] Pad016
  BaseFeature = -> Pad015
  Direction = (0,0,1)
  Length = 3.5
  Length2 = 10
  Profile = -> Sketch028
  ReferenceAxis = -> Sketch028 [N_Axis]
  Refine = true
  Reversed = true
  Suppressed = false
  Type = 0
FEATURE [Sketcher::SketchObject] Sketch029  label="ab_membrane_holders"
  ArcFitTolerance = 1e-06
  AttachmentOffset = pos=(0,0,-2) rot=(0,0,1;0rad)
  AttachmentSupport = -> [XY_Plane002]
  ExternalGeometry = -> [Sketch022]
  FullyConstrained = true
  MakeInternals = false
  MapMode = 5
  Placement = pos=(0,0,-2) rot=(0,0,1;0rad)
  expr: .AttachmentOffset.Base.z = -Spreadsheet.B1
  sketch-geometry (11):
    g0: LineSegment [constr] StartX=25.1094 StartY=-27.01 StartZ=0 EndX=11.1 EndY=-30.75 EndZ=0
    g1: LineSegment [constr] StartX=17.5429 StartY=-35.4989 StartZ=0 EndX=19.4752 EndY=-34.983 EndZ=0
    g2: LineSegment [constr] StartX=19.4752 StartY=-34.983 StartZ=0 EndX=16.2511 EndY=-22.906 EndZ=0
    g3: LineSegment [constr] StartX=16.2511 StartY=-22.906 StartZ=0 EndX=14.3187 EndY=-23.4218 EndZ=0
    g4: LineSegment [constr] StartX=14.3187 StartY=-23.4218 StartZ=0 EndX=17.5429 EndY=-35.4989 EndZ=0
    g5: LineSegment [constr] StartX=19.4752 StartY=-34.983 StartZ=0 EndX=14.3187 EndY=-23.4218 EndZ=0
    g6: LineSegment [constr] StartX=17.5429 StartY=-35.4989 StartZ=0 EndX=16.2511 EndY=-22.906 EndZ=0
    g7: GeomPoint [constr] X=16.897 Y=-29.2024 Z=0
    g8: Circle CenterX=19.4752 CenterY=-34.983 CenterZ=0 NormalX=0 NormalY=0 NormalZ=1 AngleXU=0 Radius=1.5
    g9: GeomPoint [constr] X=17.8631 Y=-28.9445 Z=0
    g10: Circle CenterX=14.3187 CenterY=-23.4218 CenterZ=0 NormalX=0 NormalY=0 NormalZ=1 AngleXU=0 Radius=0.75
  constraints (26):
    c: Coincident(g2,g1)
    c: Coincident(g4,g3)
    c: Angle(g0,g2) = 1.5708
    c: Angle(g2,g1) = 1.5708
    c: Parallel(g2,g4)
    c: Parallel(g1,g3)
    c: Distance(g4) = 12.5
    c: Coincident(g5,g1)
    c: Coincident(g5,g3)
    c: PointOnObject(g7,g5)
    c: PointOnObject(g7,g6)
    c: PointOnObject(g7,g0)
    c: Distance(g1) = 2
    c: Coincident(g8,g1)
    c: PointOnObject(g9,g2)
    c: PointOnObject(g9,g0)
    c: Distance(g9,g0) = 7
    c: Diameter(g8) = 3
    c: Coincident(g2,g3)
    c: Coincident(g6,g2)
    c: Coincident(g6,g4)
    c: Coincident(g1,g4)
    c: Diameter(g10) = 1.5
    c: Coincident(g10,g3)
    c: Coincident(g0,g-4)
    c: Coincident(g0,g-3)
FEATURE [PartDesign::Pad] Pad017
  BaseFeature = -> Pad016
  Direction = (0,0,1)
  Length = 5.5
  Length2 = 10
  Profile = -> Sketch029
  ReferenceAxis = -> Sketch029 [N_Axis]
  Refine = true
  Reversed = true
  Suppressed = false
  Type = 0
  expr: Length = Spreadsheet.B2
FEATURE [Sketcher::SketchObject] Sketch030  label="dpad_membrane_holder"
  ArcFitTolerance = 1e-06
  AttachmentOffset = pos=(0,0,-2) rot=(0,0,1;0rad)
  AttachmentSupport = -> [XY_Plane002]
  ExternalGeometry = -> [Sketch022]
  FullyConstrained = true
  MakeInternals = false
  MapMode = 5
  Placement = pos=(0,0,-2) rot=(0,0,1;0rad)
  expr: .AttachmentOffset.Base.z = -Spreadsheet.B1
  sketch-geometry (12):
    g0: LineSegment [constr] StartX=-23.25 StartY=-29.415 StartZ=0 EndX=-16.75 EndY=-35.915 EndZ=0
    g1: LineSegment [constr] StartX=-23.25 StartY=-35.915 StartZ=0 EndX=-16.75 EndY=-29.415 EndZ=0
    g2: GeomPoint [constr] X=-20 Y=-32.665 Z=0
    g3: LineSegment [constr] StartX=-8.37903 StartY=-42.54 StartZ=0 EndX=-8.37903 EndY=-22.79 EndZ=0
    g4: LineSegment [constr] StartX=-8.37903 StartY=-22.79 StartZ=0 EndX=-31.621 EndY=-22.79 EndZ=0
    g5: LineSegment [constr] StartX=-31.621 StartY=-22.79 StartZ=0 EndX=-31.621 EndY=-42.54 EndZ=0
    g6: LineSegment [constr] StartX=-31.621 StartY=-42.54 StartZ=0 EndX=-8.37903 EndY=-42.54 EndZ=0
    g7: Circle CenterX=-31.621 CenterY=-22.79 CenterZ=0 NormalX=0 NormalY=0 NormalZ=1 AngleXU=0 Radius=0.9
    g8: Circle CenterX=-8.37903 CenterY=-42.54 CenterZ=0 NormalX=0 NormalY=0 NormalZ=1 AngleXU=0 Radius=0.9
    g9: LineSegment [constr] StartX=-31.621 StartY=-22.79 StartZ=0 EndX=-8.37903 EndY=-42.54 EndZ=0
    g10: LineSegment [constr] StartX=-8.37903 StartY=-22.79 StartZ=0 EndX=-31.621 EndY=-42.54 EndZ=0
    g11: GeomPoint [constr] X=-20 Y=-32.665 Z=0
  constraints (27):
    c: Coincident(g0,g-3)
    c: Coincident(g0,g-5)
    c: Coincident(g1,g-4)
    c: Coincident(g1,g-6)
    c: PointOnObject(g2,g1)
    c: PointOnObject(g2,g0)
    c: Coincident(g3,g4)
    c: Coincident(g5,g6)
    c: Coincident(g6,g3)
    c: Horizontal(g6)
    c: Coincident(g4,g5)
    c: Coincident(g7,g4)
    c: Coincident(g8,g3)
    c: Equal(g7,g8)
    c: Diameter(g8) = 1.8
    c: Vertical(g5)
    c: Coincident(g9,g4)
    c: Coincident(g9,g3)
    c: Coincident(g10,g3)
    c: Coincident(g10,g5)
    c: PointOnObject(g11,g9)
    c: PointOnObject(g11,g10)
    c: Coincident(g11,g2)
    c: DistanceY(g5,g5) = 19.75
    c: Horizontal(g4)
    c: Vertical(g3)
    c: Distance(g9) = 30.5
FEATURE [PartDesign::Pad] Pad018
  BaseFeature = -> Pad017
  Direction = (0,0,1)
  Length = 5.5
  Length2 = 10
  Profile = -> Sketch030
  ReferenceAxis = -> Sketch030 [N_Axis]
  Refine = true
  Reversed = true
  Suppressed = false
  Type = 0
  expr: Length = Spreadsheet.B2
FEATURE [PartDesign::Fillet] Fillet007
  Base = -> Pad018 [Edge177,Edge175,Edge163,Edge165,Edge176,Edge179]
  BaseFeature = -> Pad018
  Radius = 0.75
  Refine = true
  SupportTransform = false
  Suppressed = false
  UseAllEdges = false
FEATURE [PartDesign::Pocket] Pocket009
  BaseFeature = -> Fillet007
  Direction = (0,0,-1)
  Length = 5
  Length2 = 5
  Profile = -> Sketch027
  ReferenceAxis = -> Sketch027 [N_Axis]
  Refine = true
  Suppressed = false
  Type = 0
FEATURE [Sketcher::SketchObject] Sketch031  label="status_led_socket"
  ArcFitTolerance = 1e-06
  AttachmentOffset = pos=(0,0,-2) rot=(0,0,1;0rad)
  AttachmentSupport = -> [XY_Plane002]
  ExternalGeometry = -> [Sketch022]
  FullyConstrained = true
  MakeInternals = false
  MapMode = 5
  Placement = pos=(0,0,-2) rot=(0,0,1;0rad)
  expr: .AttachmentOffset.Base.z = -Spreadsheet.B1
  sketch-geometry (14):
    g0: LineSegment StartX=-1.25 StartY=-17.25 StartZ=0 EndX=-1.25 EndY=-20.75 EndZ=0
    g1: LineSegment StartX=-1.25 StartY=-20.75 StartZ=0 EndX=1.25 EndY=-20.75 EndZ=0
    g2: LineSegment StartX=1.25 StartY=-20.75 StartZ=0 EndX=1.25 EndY=-17.25 EndZ=0
    g3: LineSegment StartX=1.25 StartY=-17.25 StartZ=0 EndX=-1.25 EndY=-17.25 EndZ=0
    g4: LineSegment [constr] StartX=-1.25 StartY=-17.25 StartZ=0 EndX=1.25 EndY=-20.75 EndZ=0
    g5: LineSegment [constr] StartX=-1.25 StartY=-20.75 StartZ=0 EndX=1.25 EndY=-17.25 EndZ=0
    g6: GeomPoint [constr] X=0 Y=-19 Z=0
    g7: LineSegment StartX=-1.25 StartY=-11.75 StartZ=0 EndX=-1.25 EndY=-15.25 EndZ=0
    g8: LineSegment StartX=-1.25 StartY=-15.25 StartZ=0 EndX=1.25 EndY=-15.25 EndZ=0
    g9: LineSegment StartX=1.25 StartY=-15.25 StartZ=0 EndX=1.25 EndY=-11.75 EndZ=0
    g10: LineSegment StartX=1.25 StartY=-11.75 StartZ=0 EndX=-1.25 EndY=-11.75 EndZ=0
    g11: LineSegment [constr] StartX=-1.25 StartY=-11.75 StartZ=0 EndX=1.25 EndY=-15.25 EndZ=0
    g12: LineSegment [constr] StartX=1.25 StartY=-11.75 StartZ=0 EndX=-1.25 EndY=-15.25 EndZ=0
    g13: GeomPoint [constr] X=0 Y=-13.5 Z=0
  constraints (34):
    c: Coincident(g0,g1)
    c: Coincident(g1,g2)
    c: Coincident(g2,g3)
    c: Coincident(g3,g0)
    c: Vertical(g0)
    c: Vertical(g2)
    c: Horizontal(g1)
    c: Horizontal(g3)
    c: Distance(g0,g2) = 2.5
    c: Distance(g1,g3) = 3.5
    c: Coincident(g4,g0)
    c: Coincident(g4,g1)
    c: PointOnObject(g6,g4)
    c: PointOnObject(g6,g5)
    c: Coincident(g5,g2)
    c: Coincident(g5,g0)
    c: Coincident(g6,g-3)
    c: Coincident(g7,g8)
    c: Coincident(g8,g9)
    c: Coincident(g9,g10)
    c: Coincident(g10,g7)
    c: Vertical(g7)
    c: Vertical(g9)
    c: Horizontal(g8)
    c: Horizontal(g10)
    c: Coincident(g11,g7)
    c: Coincident(g11,g8)
    c: Coincident(g12,g9)
    c: Coincident(g12,g7)
    c: PointOnObject(g13,g11)
    c: PointOnObject(g13,g12)
    c: Equal(g3,g10)
    c: Equal(g0,g7)
    c: Coincident(g13,g-4)
FEATURE [PartDesign::Pocket] Pocket010
  BaseFeature = -> Pocket009
  Direction = (0,0,-1)
  Length = 1
  Length2 = 5
  Profile = -> Sketch031
  ReferenceAxis = -> Sketch031 [N_Axis]
  Refine = true
  Reversed = true
  Suppressed = false
  Type = 0
FEATURE [Sketcher::SketchObject] Sketch032  label="dpad_socket2"
  ArcFitTolerance = 1e-06
  AttachmentOffset = pos=(0,0,-2) rot=(0,0,1;0rad)
  AttachmentSupport = -> [XY_Plane002]
  ExternalGeometry = -> [Sketch022]
  FullyConstrained = true
  MakeInternals = false
  MapMode = 5
  Placement = pos=(0,0,-2) rot=(0,0,1;0rad)
  expr: .AttachmentOffset.Base.z = -Spreadsheet.B1
  sketch-geometry (39):
    g0: LineSegment StartX=-29.75 StartY=-29.415 StartZ=0 EndX=-29.75 EndY=-35.915 EndZ=0
    g1: LineSegment StartX=-29.75 StartY=-35.915 StartZ=0 EndX=-23.25 EndY=-35.915 EndZ=0
    g2: LineSegment StartX=-23.25 StartY=-35.915 StartZ=0 EndX=-23.25 EndY=-42.415 EndZ=0
    g3: LineSegment StartX=-23.25 StartY=-42.415 StartZ=0 EndX=-16.75 EndY=-42.415 EndZ=0
    g4: LineSegment StartX=-16.75 StartY=-42.415 StartZ=0 EndX=-16.75 EndY=-35.915 EndZ=0
    g5: LineSegment StartX=-16.75 StartY=-35.915 StartZ=0 EndX=-10.25 EndY=-35.915 EndZ=0
    g6: LineSegment StartX=-10.25 StartY=-35.915 StartZ=0 EndX=-10.25 EndY=-29.415 EndZ=0
    g7: LineSegment StartX=-10.25 StartY=-29.415 StartZ=0 EndX=-16.75 EndY=-29.415 EndZ=0
    g8: LineSegment StartX=-16.75 StartY=-29.415 StartZ=0 EndX=-16.75 EndY=-22.915 EndZ=0
    g9: LineSegment StartX=-16.75 StartY=-22.915 StartZ=0 EndX=-23.25 EndY=-22.915 EndZ=0
    g10: LineSegment StartX=-23.25 StartY=-22.915 StartZ=0 EndX=-23.25 EndY=-29.415 EndZ=0
    g11: LineSegment StartX=-23.25 StartY=-29.415 StartZ=0 EndX=-29.75 EndY=-29.415 EndZ=0
    g12: LineSegment StartX=-31.25 StartY=-27.915 StartZ=0 EndX=-31.25 EndY=-37.415 EndZ=0
    g13: LineSegment StartX=-31.25 StartY=-37.415 StartZ=0 EndX=-24.75 EndY=-37.415 EndZ=0
    g14: LineSegment StartX=-24.75 StartY=-37.415 StartZ=0 EndX=-24.75 EndY=-43.915 EndZ=0
    g15: LineSegment StartX=-24.75 StartY=-43.915 StartZ=0 EndX=-15.25 EndY=-43.915 EndZ=0
    g16: LineSegment StartX=-15.25 StartY=-43.915 StartZ=0 EndX=-15.25 EndY=-37.415 EndZ=0
    g17: LineSegment StartX=-15.25 StartY=-37.415 StartZ=0 EndX=-8.75 EndY=-37.415 EndZ=0
    g18: LineSegment StartX=-8.75 StartY=-37.415 StartZ=0 EndX=-8.75 EndY=-27.915 EndZ=0
    g19: LineSegment StartX=-8.75 StartY=-27.915 StartZ=0 EndX=-15.25 EndY=-27.915 EndZ=0
    g20: LineSegment StartX=-15.25 StartY=-27.915 StartZ=0 EndX=-15.25 EndY=-21.415 EndZ=0
    g21: LineSegment StartX=-15.25 StartY=-21.415 StartZ=0 EndX=-24.75 EndY=-21.415 EndZ=0
    g22: LineSegment StartX=-24.75 StartY=-21.415 StartZ=0 EndX=-24.75 EndY=-27.915 EndZ=0
    g23: LineSegment StartX=-24.75 StartY=-27.915 StartZ=0 EndX=-31.25 EndY=-27.915 EndZ=0
    g24: LineSegment [constr] StartX=-24.75 StartY=-37.415 StartZ=0 EndX=-15.25 EndY=-37.415 EndZ=0
    g25: LineSegment [constr] StartX=-15.25 StartY=-37.415 StartZ=0 EndX=-15.25 EndY=-27.915 EndZ=0
    g26: LineSegment [constr] StartX=-15.25 StartY=-27.915 StartZ=0 EndX=-24.75 EndY=-27.915 EndZ=0
    g27: LineSegment [constr] StartX=-24.75 StartY=-27.915 StartZ=0 EndX=-24.75 EndY=-37.415 EndZ=0
    g28: LineSegment [constr] StartX=-31.25 StartY=-21.415 StartZ=0 EndX=-31.25 EndY=-43.915 EndZ=0
    g29: LineSegment [constr] StartX=-31.25 StartY=-43.915 StartZ=0 EndX=-8.75 EndY=-43.915 EndZ=0
    g30: LineSegment [constr] StartX=-8.75 StartY=-43.915 StartZ=0 EndX=-8.75 EndY=-21.415 EndZ=0
    g31: LineSegment [constr] StartX=-8.75 StartY=-21.415 StartZ=0 EndX=-31.25 EndY=-21.415 EndZ=0
    g32: LineSegment [constr] StartX=-24.75 StartY=-27.915 StartZ=0 EndX=-15.25 EndY=-37.415 EndZ=0
    g33: LineSegment [constr] StartX=-15.25 StartY=-27.915 StartZ=0 EndX=-24.75 EndY=-37.415 EndZ=0
    g34: GeomPoint [constr] X=-20 Y=-32.665 Z=0
    g35: LineSegment [constr] StartX=-10.25 StartY=-29.415 StartZ=0 EndX=-8.75 EndY=-29.415 EndZ=0
    g36: LineSegment [constr] StartX=-8.75 StartY=-29.415 StartZ=0 EndX=-8.75 EndY=-27.915 EndZ=0
    g37: LineSegment [constr] StartX=-8.75 StartY=-27.915 StartZ=0 EndX=-10.25 EndY=-27.915 EndZ=0
    g38: LineSegment [constr] StartX=-10.25 StartY=-27.915 StartZ=0 EndX=-10.25 EndY=-29.415 EndZ=0
  constraints (96):
    c: Coincident(g-14,g0)
    c: Coincident(g0,g-14)
    c: Coincident(g0,g1)
    c: Coincident(g1,g-13)
    c: Coincident(g1,g2)
    c: Coincident(g2,g-12)
    c: Coincident(g2,g3)
    c: Coincident(g3,g-11)
    c: Coincident(g3,g4)
    c: Coincident(g4,g-10)
    c: Coincident(g4,g5)
    c: Coincident(g5,g-9)
    c: Coincident(g5,g6)
    c: Coincident(g6,g-8)
    c: Coincident(g6,g7)
    c: Coincident(g7,g-7)
    c: Coincident(g7,g8)
    c: Coincident(g8,g-6)
    c: Coincident(g8,g9)
    c: Coincident(g9,g-5)
    c: Coincident(g9,g10)
    c: Coincident(g10,g-4)
    c: Coincident(g10,g11)
    c: Coincident(g11,g0)
    c: Vertical(g12)
    c: Coincident(g12,g13)
    c: Horizontal(g13)
    c: Coincident(g13,g14)
    c: Vertical(g14)
    c: Coincident(g14,g15)
    c: Horizontal(g15)
    c: Coincident(g15,g16)
    c: Coincident(g16,g17)
    c: Horizontal(g17)
    c: Coincident(g17,g18)
    c: Vertical(g18)
    c: Coincident(g18,g19)
    c: Coincident(g19,g20)
    c: Vertical(g20)
    c: Coincident(g20,g21)
    c: Horizontal(g21)
    c: Coincident(g21,g22)
    c: Vertical(g22)
    c: Coincident(g22,g23)
    c: Coincident(g23,g12)
    c: Horizontal(g23)
    c: Horizontal(g19)
    c: Vertical(g16)
    c: Coincident(g24,g25)
    c: Coincident(g25,g26)
    c: Coincident(g26,g27)
    c: Coincident(g27,g24)
    c: Horizontal(g24)
    c: Horizontal(g26)
    c: Vertical(g25)
    c: Vertical(g27)
    c: Coincident(g24,g13)
    c: Coincident(g25,g19)
    c: Coincident(g22,g26)
    c: Coincident(g16,g24)
    c: Coincident(g28,g29)
    c: Coincident(g29,g30)
    c: Coincident(g30,g31)
    c: Coincident(g31,g28)
    c: Vertical(g28)
    c: Vertical(g30)
    c: Horizontal(g29)
    c: Horizontal(g31)
    c: PointOnObject(g12,g28)
    c: PointOnObject(g21,g31)
    c: PointOnObject(g15,g29)
    c: PointOnObject(g17,g30)
    c: Coincident(g32,g22)
    c: Coincident(g32,g16)
    c: Coincident(g33,g19)
    c: Coincident(g33,g13)
    c: PointOnObject(g34,g32)
    c: PointOnObject(g34,g33)
    c: Equal(g28,g29)
    c: Equal(g27,g26)
    c: PointOnObject(g7,g33)
    c: Equal(g23,g22)
    c: Equal(g20,g19)
    c: PointOnObject(g10,g32)
    c: Coincident(g35,g36)
    c: Coincident(g36,g37)
    c: Coincident(g37,g38)
    c: Coincident(g38,g35)
    c: Horizontal(g35)
    c: Horizontal(g37)
    c: Vertical(g36)
    c: Vertical(g38)
    c: Coincident(g35,g6)
    c: Coincident(g36,g18)
    c: Equal(g38,g35)
    c: DistanceX(g35,g35) = 1.5
FEATURE [PartDesign::Pad] Pad019
  BaseFeature = -> Pocket010
  Direction = (0,0,1)
  Length = 0.1
  Length2 = 10
  Profile = -> Sketch032
  ReferenceAxis = -> Sketch032 [N_Axis]
  Refine = true
  Reversed = true
  Suppressed = false
  Type = 0
FEATURE [Sketcher::SketchObject] Sketch033  label="speaker_socket"
  ArcFitTolerance = 1e-06
  AttachmentOffset = pos=(0,0,-2) rot=(0,0,1;0rad)
  AttachmentSupport = -> [XY_Plane002]
  FullyConstrained = false
  MakeInternals = false
  MapMode = 5
  Placement = pos=(0,0,-2) rot=(0,0,1;0rad)
  expr: .AttachmentOffset.Base.z = -Spreadsheet.B1
  sketch-geometry (2):
    g0: Circle CenterX=-20.6756 CenterY=-58.3228 CenterZ=0 NormalX=0 NormalY=0 NormalZ=1 AngleXU=0 Radius=10.75
    g1: Circle CenterX=-20.6756 CenterY=-58.3228 CenterZ=0 NormalX=0 NormalY=0 NormalZ=1 AngleXU=0 Radius=11.75
  constraints (3):
    c: Diameter(g0) = 21.5
    c: Coincident(g1,g0)
    c: Diameter(g1) = 23.5
FEATURE [PartDesign::Pad] Pad020
  BaseFeature = -> Pad019
  Direction = (0,0,1)
  Length = 3
  Length2 = 10
  Profile = -> Sketch033
  ReferenceAxis = -> Sketch033 [N_Axis]
  Refine = true
  Reversed = true
  Suppressed = false
  Type = 0
FEATURE [Sketcher::SketchObject] Sketch034  label="speaker_holes_0"
  ArcFitTolerance = 1e-06
  AttachmentSupport = -> [XY_Plane002]
  ExternalGeometry = -> [Sketch033]
  FullyConstrained = false
  MakeInternals = false
  MapMode = 5
  sketch-geometry (1):
    g0: Circle CenterX=-20.6756 CenterY=-58.3228 CenterZ=0 NormalX=0 NormalY=0 NormalZ=1 AngleXU=0 Radius=0.75
FEATURE [Sketcher::SketchObject] Sketch036  label="speaker_holes_1"
  ArcFitTolerance = 1e-06
  AttachmentSupport = -> [XY_Plane002]
  ExternalGeometry = -> [Sketch034]
  FullyConstrained = true
  MakeInternals = false
  MapMode = 5
  sketch-geometry (3):
    g0: Circle CenterX=-20.6756 CenterY=-55.8228 CenterZ=0 NormalX=0 NormalY=0 NormalZ=1 AngleXU=0 Radius=0.75
    g1: LineSegment [constr] StartX=-20.6756 StartY=-55.8228 StartZ=0 EndX=-20.6756 EndY=-58.3228 EndZ=0
    g2: Circle CenterX=-20.6756 CenterY=-58.3228 CenterZ=0 NormalX=0 NormalY=0 NormalZ=1 AngleXU=0 Radius=0.75
  constraints (7):
    c: Diameter(g0) = 1.5
    c: Coincident(g1,g0)
    c: Coincident(g1,g-3)
    c: Vertical(g1)
    c: DistanceY(g1,g1) = 2.5
    c: Coincident(g2,g1)
    c: Equal(g-3,g2)
FEATURE [Sketcher::SketchObject] Sketch037  label="speaker_holes_2"
  ArcFitTolerance = 1e-06
  AttachmentSupport = -> [XY_Plane002]
  ExternalGeometry = -> [Sketch036]
  FullyConstrained = true
  MakeInternals = false
  MapMode = 5
  sketch-geometry (2):
    g0: Circle CenterX=-20.6756 CenterY=-53.3228 CenterZ=0 NormalX=0 NormalY=0 NormalZ=1 AngleXU=0 Radius=0.75
    g1: LineSegment [constr] StartX=-20.6756 StartY=-53.3228 StartZ=0 EndX=-20.6756 EndY=-55.8228 EndZ=0
  constraints (5):
    c: Diameter(g0) = 1.5
    c: Coincident(g1,g0)
    c: Coincident(g1,g-3)
    c: Vertical(g1)
    c: DistanceY(g1,g1) = 2.5
FEATURE [Sketcher::SketchObject] Sketch038  label="speaker_holes_3"
  ArcFitTolerance = 1e-06
  AttachmentSupport = -> [XY_Plane002]
  ExternalGeometry = -> [Sketch037]
  FullyConstrained = true
  MakeInternals = false
  MapMode = 5
  sketch-geometry (2):
    g0: Circle CenterX=-20.6756 CenterY=-50.8228 CenterZ=0 NormalX=0 NormalY=0 NormalZ=1 AngleXU=0 Radius=0.75
    g1: LineSegment [constr] StartX=-20.6756 StartY=-50.8228 StartZ=0 EndX=-20.6756 EndY=-53.3228 EndZ=0
  constraints (5):
    c: Diameter(g0) = 1.5
    c: Coincident(g1,g0)
    c: Coincident(g1,g-3)
    c: Vertical(g1)
    c: DistanceY(g1,g1) = 2.5
FEATURE [PartDesign::Pocket] Pocket011
  BaseFeature = -> Pad020
  Direction = (0,0,-1)
  Length = 5
  Length2 = 5
  Profile = -> Sketch036
  ReferenceAxis = -> Sketch036 [N_Axis]
  Refine = true
  Suppressed = false
  Type = 0
FEATURE [PartDesign::PolarPattern] PolarPattern
  Angle = 360
  Axis = -> Pocket011 [Edge372]
  BaseFeature = -> Pocket011
  Mode = 0
  Occurrences = 6
  Offset = 120
  Originals = -> [Pocket011]
  Refine = true
  Suppressed = false
  TransformMode = 0
FEATURE [PartDesign::Pocket] Pocket012
  BaseFeature = -> PolarPattern
  Direction = (0,0,-1)
  Length = 5
  Length2 = 5
  Profile = -> Sketch037
  ReferenceAxis = -> Sketch037 [N_Axis]
  Refine = true
  Suppressed = false
  Type = 0
FEATURE [PartDesign::PolarPattern] PolarPattern001
  Angle = 360
  Axis = -> Pocket012 [Edge261]
  BaseFeature = -> Pocket012
  Mode = 0
  Occurrences = 12
  Offset = 120
  Originals = -> [Pocket012]
  Refine = true
  Suppressed = false
  TransformMode = 0
FEATURE [PartDesign::Pocket] Pocket013
  BaseFeature = -> PolarPattern001
  Direction = (0,0,-1)
  Length = 5
  Length2 = 5
  Profile = -> Sketch038
  ReferenceAxis = -> Sketch038 [N_Axis]
  Refine = true
  Suppressed = false
  Type = 0
FEATURE [PartDesign::PolarPattern] PolarPattern002
  Angle = 360
  Axis = -> Pocket013 [Edge267]
  BaseFeature = -> Pocket013
  Mode = 0
  Occurrences = 16
  Offset = 120
  Originals = -> [Pocket013]
  Refine = true
  Suppressed = false
  TransformMode = 0
FEATURE [Sketcher::SketchObject] Sketch039  label="display_frame001"
  ArcFitTolerance = 1e-06
  AttachmentOffset = pos=(0,0,-2) rot=(0,0,1;0rad)
  AttachmentSupport = -> [XY_Plane002]
  ExternalGeometry = -> [Sketch022]
  FullyConstrained = true
  MakeInternals = false
  MapMode = 5
  Placement = pos=(0,0,-2) rot=(0,0,1;0rad)
  expr: .AttachmentOffset.Base.z = -Spreadsheet.B1
  sketch-geometry (38):
    g0: LineSegment [constr] StartX=-24.75 StartY=36 StartZ=0 EndX=-24.75 EndY=-1.5 EndZ=0
    g1: LineSegment [constr] StartX=-24.75 StartY=-1.5 StartZ=0 EndX=24.75 EndY=-1.5 EndZ=0
    g2: LineSegment [constr] StartX=24.75 StartY=-1.5 StartZ=0 EndX=24.75 EndY=36 EndZ=0
    g3: LineSegment [constr] StartX=24.75 StartY=36 StartZ=0 EndX=-24.75 EndY=36 EndZ=0
    g4: LineSegment StartX=-34.95 StartY=36.8 StartZ=0 EndX=-33.45 EndY=36.8 EndZ=0
    g5: LineSegment StartX=-33.45 StartY=36.8 StartZ=0 EndX=-33.45 EndY=38.8 EndZ=0
    g6: LineSegment StartX=-33.45 StartY=38.8 StartZ=0 EndX=27.55 EndY=38.8 EndZ=0
    g7: LineSegment StartX=27.55 StartY=38.8 StartZ=0 EndX=27.55 EndY=-4.3 EndZ=0
    g8: LineSegment StartX=27.55 StartY=-4.3 StartZ=0 EndX=-33.45 EndY=-4.3 EndZ=0
    g9: LineSegment StartX=-33.45 StartY=-4.3 StartZ=0 EndX=-33.45 EndY=-2.3 EndZ=0
    g10: LineSegment StartX=-33.45 StartY=-2.3 StartZ=0 EndX=-34.95 EndY=-2.3 EndZ=0
    g11: LineSegment StartX=-34.95 StartY=-2.3 StartZ=0 EndX=-34.95 EndY=-5.8 EndZ=0
    g12: LineSegment StartX=-34.95 StartY=-5.8 StartZ=0 EndX=29.05 EndY=-5.8 EndZ=0
    g13: LineSegment StartX=29.05 StartY=-5.8 StartZ=0 EndX=29.05 EndY=40.3 EndZ=0
    g14: LineSegment StartX=29.05 StartY=40.3 StartZ=0 EndX=-34.95 EndY=40.3 EndZ=0
    g15: LineSegment StartX=-34.95 StartY=40.3 StartZ=0 EndX=-34.95 EndY=36.8 EndZ=0
    g16: LineSegment [constr] StartX=-34.95 StartY=40.3 StartZ=0 EndX=-34.95 EndY=38.8 EndZ=0
    g17: LineSegment [constr] StartX=-34.95 StartY=38.8 StartZ=0 EndX=-33.45 EndY=38.8 EndZ=0
    g18: LineSegment [constr] StartX=-33.45 StartY=38.8 StartZ=0 EndX=-33.45 EndY=40.3 EndZ=0
    g19: LineSegment [constr] StartX=-33.45 StartY=40.3 StartZ=0 EndX=-34.95 EndY=40.3 EndZ=0
    g20: LineSegment [constr] StartX=27.55 StartY=38.8 StartZ=0 EndX=29.05 EndY=38.8 EndZ=0
    g21: LineSegment [constr] StartX=29.05 StartY=38.8 StartZ=0 EndX=29.05 EndY=40.3 EndZ=0
    g22: LineSegment [constr] StartX=29.05 StartY=40.3 StartZ=0 EndX=27.55 EndY=40.3 EndZ=0
    g23: LineSegment [constr] StartX=27.55 StartY=40.3 StartZ=0 EndX=27.55 EndY=38.8 EndZ=0
    g24: LineSegment [constr] StartX=27.55 StartY=-4.3 StartZ=0 EndX=27.55 EndY=-5.8 EndZ=0
    g25: LineSegment [constr] StartX=27.55 StartY=-5.8 StartZ=0 EndX=29.05 EndY=-5.8 EndZ=0
    g26: LineSegment [constr] StartX=29.05 StartY=-5.8 StartZ=0 EndX=29.05 EndY=-4.3 EndZ=0
    g27: LineSegment [constr] StartX=29.05 StartY=-4.3 StartZ=0 EndX=27.55 EndY=-4.3 EndZ=0
    g28: LineSegment [constr] StartX=-33.45 StartY=-4.3 StartZ=0 EndX=-34.95 EndY=-4.3 EndZ=0
    g29: LineSegment [constr] StartX=-34.95 StartY=-4.3 StartZ=0 EndX=-34.95 EndY=-5.8 EndZ=0
    g30: LineSegment [constr] StartX=-34.95 StartY=-5.8 StartZ=0 EndX=-33.45 EndY=-5.8 EndZ=0
    g31: LineSegment [constr] StartX=-33.45 StartY=-5.8 StartZ=0 EndX=-33.45 EndY=-4.3 EndZ=0
    g32: LineSegment [constr] StartX=24.75 StartY=36 StartZ=0 EndX=27.55 EndY=36 EndZ=0
    g33: LineSegment [constr] StartX=27.55 StartY=36 StartZ=0 EndX=27.55 EndY=38.8 EndZ=0
    g34: LineSegment [constr] StartX=27.55 StartY=38.8 StartZ=0 EndX=24.75 EndY=38.8 EndZ=0
    g35: LineSegment [constr] StartX=24.75 StartY=38.8 StartZ=0 EndX=24.75 EndY=36 EndZ=0
    g36: LineSegment [constr] StartX=-33.45 StartY=36.8 StartZ=0 EndX=-33.45 EndY=-2.3 EndZ=0
    g37: LineSegment [constr] StartX=24.75 StartY=-1.5 StartZ=0 EndX=24.75 EndY=-4.3 EndZ=0
  constraints (101):
    c: Coincident(g0,g1)
    c: Coincident(g1,g2)
    c: Coincident(g2,g3)
    c: Coincident(g3,g0)
    c: Vertical(g0)
    c: Vertical(g2)
    c: Horizontal(g1)
    c: Horizontal(g3)
    c: Coincident(g0,g-3)
    c: Coincident(g1,g-4)
    c: Horizontal(g4)
    c: Coincident(g4,g5)
    c: Vertical(g5)
    c: Coincident(g5,g6)
    c: Horizontal(g6)
    c: Coincident(g6,g7)
    c: Vertical(g7)
    c: Coincident(g7,g8)
    c: Horizontal(g8)
    c: Coincident(g8,g9)
    c: Vertical(g9)
    c: Coincident(g9,g10)
    c: Horizontal(g10)
    c: Coincident(g10,g11)
    c: Vertical(g11)
    c: Coincident(g11,g12)
    c: Horizontal(g12)
    c: Coincident(g12,g13)
    c: Vertical(g13)
    c: Coincident(g13,g14)
    c: Horizontal(g14)
    c: Coincident(g14,g15)
    c: Coincident(g15,g4)
    c: Vertical(g15)
    c: Coincident(g16,g17)
    c: Coincident(g17,g18)
    c: Coincident(g18,g19)
    c: Coincident(g19,g16)
    c: Vertical(g16)
    c: Vertical(g18)
    c: Horizontal(g17)
    c: Horizontal(g19)
    c: Coincident(g16,g14)
    c: Coincident(g17,g5)
    c: Coincident(g20,g21)
    c: Coincident(g21,g22)
    c: Coincident(g22,g23)
    c: Coincident(g23,g20)
    c: Horizontal(g20)
    c: Horizontal(g22)
    c: Vertical(g21)
    c: Vertical(g23)
    c: Coincident(g20,g6)
    c: Coincident(g21,g13)
    c: Coincident(g24,g25)
    c: Coincident(g25,g26)
    c: Coincident(g26,g27)
    c: Coincident(g27,g24)
    c: Vertical(g24)
    c: Vertical(g26)
    c: Horizontal(g25)
    c: Horizontal(g27)
    c: Coincident(g24,g7)
    c: Coincident(g25,g12)
    c: Coincident(g28,g29)
    c: Coincident(g29,g30)
    c: Coincident(g30,g31)
    c: Coincident(g31,g28)
    c: Horizontal(g28)
    c: Horizontal(g30)
    c: Vertical(g29)
    c: Vertical(g31)
    c: Coincident(g28,g8)
    c: Coincident(g29,g11)
    c: Equal(g18,g17)
    c: Equal(g17,g28)
    c: Equal(g28,g31)
    c: Equal(g31,g27)
    c: Coincident(g32,g33)
    c: Coincident(g33,g34)
    c: Coincident(g34,g35)
    c: Coincident(g35,g32)
    c: Horizontal(g32)
    c: Horizontal(g34)
    c: Vertical(g33)
    c: Vertical(g35)
    c: Coincident(g32,g2)
    c: Coincident(g33,g6)
    c: DistanceX(g32,g32) = 2.8
    c: DistanceX(g5,g6) = 61
    c: DistanceY(g8,g5) = 43.1
    c: Coincident(g36,g4)
    c: Coincident(g36,g9)
    c: Vertical(g36)
    c: DistanceY(g16,g14) = 1.5
    c: Equal(g5,g9)
    c: DistanceY(g9,g9) = 2
    c: Coincident(g37,g1)
    c: PointOnObject(g37,g8)
    c: Vertical(g37)
    c: Equal(g35,g37)
FEATURE [PartDesign::Pad] Pad021
  BaseFeature = -> PolarPattern002
  Direction = (0,0,1)
  Length = 2.5
  Length2 = 10
  Profile = -> Sketch039
  ReferenceAxis = -> Sketch039 [N_Axis]
  Refine = true
  Reversed = true
  Suppressed = false
  Type = 0
FEATURE [PartDesign::Fillet] Fillet008
  Base = -> Pad021 [Edge245,Edge247,Edge243,Edge240,Edge241,Edge249]
  BaseFeature = -> Pad021
  Radius = 1
  Refine = true
  SupportTransform = false
  Suppressed = false
  UseAllEdges = false
FEATURE [Sketcher::SketchObject] Sketch040  label="skrews_nopcb"
  ArcFitTolerance = 1e-06
  AttachmentOffset = pos=(0,0,-2) rot=(0,0,1;0rad)
  AttachmentSupport = -> [XY_Plane002]
  ExternalGeometry = -> [Sketch021]
  FullyConstrained = false
  MakeInternals = false
  MapMode = 5
  Placement = pos=(0,0,-2) rot=(0,0,1;0rad)
  expr: .AttachmentOffset.Base.z = -Spreadsheet.B1
  sketch-geometry (14):
    g0: LineSegment [constr] StartX=-32.525 StartY=-45 StartZ=0 EndX=-32.525 EndY=-67.5 EndZ=0
    g1: LineSegment [constr] StartX=32.525 StartY=-45 StartZ=0 EndX=-32.525 EndY=-45 EndZ=0
    g2: LineSegment [constr] StartX=32.525 StartY=-35 StartZ=0 EndX=32.525 EndY=-45 EndZ=0
    g3: Circle CenterX=-32.525 CenterY=-67.5 CenterZ=0 NormalX=0 NormalY=0 NormalZ=1 AngleXU=0 Radius=2.25
    g4: Circle CenterX=-32.525 CenterY=-67.5 CenterZ=0 NormalX=0 NormalY=0 NormalZ=1 AngleXU=0 Radius=0.95
    g5: LineSegment [constr] StartX=-32.525 StartY=45 StartZ=0 EndX=-32.525 EndY=-35 EndZ=0
    g6: LineSegment [constr] StartX=-32.525 StartY=-35 StartZ=0 EndX=32.525 EndY=-35 EndZ=0
    g7: LineSegment [constr] StartX=32.525 StartY=-35 StartZ=0 EndX=32.525 EndY=45 EndZ=0
    g8: LineSegment [constr] StartX=32.525 StartY=45 StartZ=0 EndX=-32.525 EndY=45 EndZ=0
    g9: Circle CenterX=32.525 CenterY=45 CenterZ=0 NormalX=0 NormalY=0 NormalZ=1 AngleXU=0 Radius=2.25
    g10: Circle CenterX=32.525 CenterY=45 CenterZ=0 NormalX=0 NormalY=0 NormalZ=1 AngleXU=0 Radius=0.95
    g11: LineSegment [constr] StartX=-32.525 StartY=-67.5 StartZ=0 EndX=-9.525 EndY=-67.5 EndZ=0
    g12: Circle CenterX=-9.525 CenterY=-67.5 CenterZ=0 NormalX=0 NormalY=0 NormalZ=1 AngleXU=0 Radius=0.95
    g13: Circle CenterX=-9.525 CenterY=-67.5 CenterZ=0 NormalX=0 NormalY=0 NormalZ=1 AngleXU=0 Radius=2.25
  constraints (32):
    c: Coincident(g1,g0)
    c: Vertical(g0)
    c: Horizontal(g1)
    c: Coincident(g0,g-3)
    c: Coincident(g2,g-4)
    c: Vertical(g2)
    c: DistanceY(g0,g0) = 22.5
    c: Coincident(g3,g0)
    c: Coincident(g4,g0)
    c: Equal(g-3,g4)
    c: Equal(g-5,g3)
    c: Coincident(g5,g6)
    c: Coincident(g6,g7)
    c: Coincident(g7,g8)
    c: Coincident(g8,g5)
    c: Vertical(g5)
    c: Vertical(g7)
    c: Horizontal(g6)
    c: Horizontal(g8)
    c: Coincident(g5,g-6)
    c: Coincident(g6,g2)
    c: Coincident(g9,g7)
    c: Coincident(g10,g7)
    c: Equal(g-3,g10)
    c: Equal(g-5,g9)
    c: Distance(g11) = 23
    c: Coincident(g11,g0)
    c: Horizontal(g11)
    c: Coincident(g12,g11)
    c: Equal(g4,g12)
    c: Equal(g3,g13)
    c: Coincident(g13,g11)
FEATURE [PartDesign::Pad] Pad022
  BaseFeature = -> Fillet008
  Direction = (0,0,1)
  Length = 7.1
  Length2 = 10
  Profile = -> Sketch040
  ReferenceAxis = -> Sketch040 [N_Axis]
  Refine = true
  Reversed = true
  Suppressed = false
  Type = 0
  expr: Length = Spreadsheet.B2 + Spreadsheet.B3
FEATURE [Sketcher::SketchObject] Sketch041  label="battery_stub"
  ArcFitTolerance = 1e-06
  AttachmentOffset = pos=(14,-54,-2) rot=(0,0,1;0rad)
  AttachmentSupport = -> [XY_Plane002]
  FullyConstrained = true
  MakeInternals = false
  MapMode = 5
  Placement = pos=(14,-54,-2) rot=(0,0,1;0rad)
  expr: .AttachmentOffset.Base.z = -Spreadsheet.B1
  sketch-geometry (4):
    g0: LineSegment StartX=-20 StartY=15.5 StartZ=0 EndX=-20 EndY=-15.5 EndZ=0
    g1: LineSegment StartX=-20 StartY=-15.5 StartZ=0 EndX=20 EndY=-15.5 EndZ=0
    g2: LineSegment StartX=20 StartY=-15.5 StartZ=0 EndX=20 EndY=15.5 EndZ=0
    g3: LineSegment StartX=20 StartY=15.5 StartZ=0 EndX=-20 EndY=15.5 EndZ=0
  constraints (11):
    c: Coincident(g0,g1)
    c: Coincident(g1,g2)
    c: Coincident(g2,g3)
    c: Coincident(g3,g0)
    c: Vertical(g0)
    c: Vertical(g2)
    c: Horizontal(g1)
    c: Horizontal(g3)
    c: Distance(g0,g2) = 40
    c: Distance(g1,g3) = 31
    c: Symmetric(g0,g1,g-1)
FEATURE [Sketcher::SketchObject] Sketch042
  ArcFitTolerance = 1e-06
  AttachmentOffset = pos=(0,0,-7.5) rot=(0,0,1;0rad)
  AttachmentSupport = -> [XY_Plane002]
  ExternalGeometry = -> [Sketch022]
  FullyConstrained = true
  MakeInternals = false
  MapMode = 5
  Placement = pos=(0,0,-7.5) rot=(0,0,1;0rad)
  expr: .AttachmentOffset.Base.z = -Spreadsheet.B1 - Spreadsheet.B2
  sketch-geometry (16):
    g0: LineSegment StartX=-35.5 StartY=48.25 StartZ=0 EndX=35.5 EndY=48.25 EndZ=0
    g1: LineSegment StartX=35.5 StartY=48.25 StartZ=0 EndX=35.5 EndY=-70.75 EndZ=0
    g2: LineSegment StartX=35.5 StartY=-70.75 StartZ=0 EndX=-35.5 EndY=-70.75 EndZ=0
    g3: LineSegment StartX=-35.5 StartY=-70.75 StartZ=0 EndX=-35.5 EndY=48.25 EndZ=0
    g4: LineSegment StartX=-36.5 StartY=49.25 StartZ=0 EndX=-36.5 EndY=-71.75 EndZ=0
    g5: LineSegment StartX=-36.5 StartY=-71.75 StartZ=0 EndX=36.5 EndY=-71.75 EndZ=0
    g6: LineSegment StartX=36.5 StartY=-71.75 StartZ=0 EndX=36.5 EndY=49.25 EndZ=0
    g7: LineSegment StartX=36.5 StartY=49.25 StartZ=0 EndX=-36.5 EndY=49.25 EndZ=0
    g8: LineSegment [constr] StartX=-36.5 StartY=49.25 StartZ=0 EndX=-36.5 EndY=48.25 EndZ=0
    g9: LineSegment [constr] StartX=-36.5 StartY=48.25 StartZ=0 EndX=-35.5 EndY=48.25 EndZ=0
    g10: LineSegment [constr] StartX=-35.5 StartY=48.25 StartZ=0 EndX=-35.5 EndY=49.25 EndZ=0
    g11: LineSegment [constr] StartX=-35.5 StartY=49.25 StartZ=0 EndX=-36.5 EndY=49.25 EndZ=0
    g12: LineSegment [constr] StartX=35.5 StartY=-70.75 StartZ=0 EndX=35.5 EndY=-71.75 EndZ=0
    g13: LineSegment [constr] StartX=35.5 StartY=-71.75 StartZ=0 EndX=36.5 EndY=-71.75 EndZ=0
    g14: LineSegment [constr] StartX=36.5 StartY=-71.75 StartZ=0 EndX=36.5 EndY=-70.75 EndZ=0
    g15: LineSegment [constr] StartX=36.5 StartY=-70.75 StartZ=0 EndX=35.5 EndY=-70.75 EndZ=0
  constraints (40):
    c: Coincident(g-4,g0)
    c: Coincident(g0,g-6)
    c: Coincident(g0,g1)
    c: Coincident(g1,g-6)
    c: Coincident(g1,g2)
    c: Coincident(g2,g-5)
    c: Coincident(g2,g3)
    c: Coincident(g3,g0)
    c: Vertical(g4)
    c: Coincident(g4,g5)
    c: Horizontal(g5)
    c: Coincident(g5,g6)
    c: Vertical(g6)
    c: Coincident(g6,g7)
    c: Coincident(g7,g4)
    c: Horizontal(g7)
    c: Coincident(g8,g9)
    c: Coincident(g9,g10)
    c: Coincident(g10,g11)
    c: Coincident(g11,g8)
    c: Vertical(g8)
    c: Vertical(g10)
    c: Horizontal(g9)
    c: Horizontal(g11)
    c: Coincident(g8,g4)
    c: Coincident(g9,g0)
    c: Coincident(g12,g13)
    c: Coincident(g13,g14)
    c: Coincident(g14,g15)
    c: Coincident(g15,g12)
    c: Vertical(g12)
    c: Vertical(g14)
    c: Horizontal(g13)
    c: Horizontal(g15)
    c: Coincident(g12,g1)
    c: Coincident(g13,g5)
    c: Equal(g12,g15)
    c: Equal(g9,g10)
    c: Equal(g15,g9)
    c: DistanceX(g9,g9) = 1
FEATURE [PartDesign::Pocket] Pocket014
  BaseFeature = -> Pad022
  Direction = (0,0,-1)
  Length = 1.5
  Length2 = 5
  Profile = -> Sketch042
  ReferenceAxis = -> Sketch042 [N_Axis]
  Refine = true
  Reversed = true
  Suppressed = false
  Type = 0
FEATURE [PartDesign::Fillet] Fillet009
  Base = -> Pocket014 [Edge426,Edge421,Edge424,Edge422]
  BaseFeature = -> Pocket014
  Radius = 1
  Refine = true
  SupportTransform = false
  Suppressed = false
  UseAllEdges = false
FEATURE [PartDesign::SubShapeBinder] Binder001
  BindCopyOnChange = 0
  BindMode = 0
  ClaimChildren = false
  Context = -> Body003 [Binder001.]
  Fuse = false
  MakeFace = true
  OffsetFill = false
  OffsetIntersection = false
  OffsetJoinType = 0
  OffsetOpenResult = false
  PartialLoad = false
  Refine = true
  Relative = true
  Support = -> [Body002[Sketch022.]]
  _Version = 2
FEATURE [PartDesign::SubShapeBinder] Binder002
  BindCopyOnChange = 0
  BindMode = 0
  ClaimChildren = false
  Context = -> Body003 [Binder002.]
  Fuse = false
  MakeFace = true
  OffsetFill = false
  OffsetIntersection = false
  OffsetJoinType = 0
  OffsetOpenResult = false
  PartialLoad = false
  Refine = true
  Relative = true
  Support = -> [Body002[Sketch021.]]
  _Version = 2
FEATURE [Sketcher::SketchObject] Sketch043  label="main001"
  ArcFitTolerance = 1e-06
  AttachmentSupport = -> [XY_Plane003]
  ExternalGeometry = -> [Binder001]
  FullyConstrained = true
  MakeInternals = false
  MapMode = 5
  sketch-geometry (4):
    g0: LineSegment StartX=-35.5 StartY=48.25 StartZ=0 EndX=-35.5 EndY=-70.75 EndZ=0
    g1: LineSegment StartX=-35.5 StartY=-70.75 StartZ=0 EndX=35.5 EndY=-70.75 EndZ=0
    g2: LineSegment StartX=35.5 StartY=-70.75 StartZ=0 EndX=35.5 EndY=48.25 EndZ=0
    g3: LineSegment StartX=35.5 StartY=48.25 StartZ=0 EndX=-35.5 EndY=48.25 EndZ=0
  constraints (10):
    c: Coincident(g0,g1)
    c: Coincident(g1,g2)
    c: Coincident(g2,g3)
    c: Coincident(g3,g0)
    c: Vertical(g0)
    c: Vertical(g2)
    c: Horizontal(g1)
    c: Horizontal(g3)
    c: Coincident(g0,g-5)
    c: Coincident(g1,g-6)
FEATURE [Sketcher::SketchObject] Sketch044  label="border001"
  ArcFitTolerance = 1e-06
  AttachmentSupport = -> [XY_Plane003]
  ExternalGeometry = -> [Sketch043]
  FullyConstrained = true
  MakeInternals = false
  MapMode = 5
  expr: Constraints[40] = Spreadsheet.B1
  sketch-geometry (16):
    g0: LineSegment StartX=-35.5 StartY=48.25 StartZ=0 EndX=-35.5 EndY=-70.75 EndZ=0
    g1: LineSegment StartX=-35.5 StartY=-70.75 StartZ=0 EndX=35.5 EndY=-70.75 EndZ=0
    g2: LineSegment StartX=35.5 StartY=-70.75 StartZ=0 EndX=35.5 EndY=48.25 EndZ=0
    g3: LineSegment StartX=35.5 StartY=48.25 StartZ=0 EndX=-35.5 EndY=48.25 EndZ=0
    g4: LineSegment StartX=-37.5 StartY=50.25 StartZ=0 EndX=-37.5 EndY=-72.75 EndZ=0
    g5: LineSegment StartX=-37.5 StartY=-72.75 StartZ=0 EndX=37.5 EndY=-72.75 EndZ=0
    g6: LineSegment StartX=37.5 StartY=-72.75 StartZ=0 EndX=37.5 EndY=50.25 EndZ=0
    g7: LineSegment StartX=37.5 StartY=50.25 StartZ=0 EndX=-37.5 EndY=50.25 EndZ=0
    g8: LineSegment [constr] StartX=-37.5 StartY=50.25 StartZ=0 EndX=-37.5 EndY=48.25 EndZ=0
    g9: LineSegment [constr] StartX=-37.5 StartY=48.25 StartZ=0 EndX=-35.5 EndY=48.25 EndZ=0
    g10: LineSegment [constr] StartX=-35.5 StartY=48.25 StartZ=0 EndX=-35.5 EndY=50.25 EndZ=0
    g11: LineSegment [constr] StartX=-35.5 StartY=50.25 StartZ=0 EndX=-37.5 EndY=50.25 EndZ=0
    g12: LineSegment [constr] StartX=35.5 StartY=-70.75 StartZ=0 EndX=35.5 EndY=-72.75 EndZ=0
    g13: LineSegment [constr] StartX=35.5 StartY=-72.75 StartZ=0 EndX=37.5 EndY=-72.75 EndZ=0
    g14: LineSegment [constr] StartX=37.5 StartY=-72.75 StartZ=0 EndX=37.5 EndY=-70.75 EndZ=0
    g15: LineSegment [constr] StartX=37.5 StartY=-70.75 StartZ=0 EndX=35.5 EndY=-70.75 EndZ=0
  constraints (42):
    c: Coincident(g0,g1)
    c: Coincident(g1,g2)
    c: Coincident(g2,g3)
    c: Coincident(g3,g0)
    c: Vertical(g0)
    c: Vertical(g2)
    c: Horizontal(g1)
    c: Horizontal(g3)
    c: Coincident(g0,g-4)
    c: Coincident(g1,g-6)
    c: Coincident(g4,g5)
    c: Coincident(g5,g6)
    c: Coincident(g6,g7)
    c: Coincident(g7,g4)
    c: Vertical(g4)
    c: Vertical(g6)
    c: Horizontal(g5)
    c: Horizontal(g7)
    c: Coincident(g8,g9)
    c: Coincident(g9,g10)
    c: Coincident(g10,g11)
    c: Coincident(g11,g8)
    c: Vertical(g8)
    c: Vertical(g10)
    c: Horizontal(g9)
    c: Horizontal(g11)
    c: Coincident(g8,g4)
    c: Coincident(g9,g0)
    c: Coincident(g12,g13)
    c: Coincident(g13,g14)
    c: Coincident(g14,g15)
    c: Coincident(g15,g12)
    c: Vertical(g12)
    c: Vertical(g14)
    c: Horizontal(g13)
    c: Horizontal(g15)
    c: Coincident(g12,g1)
    c: Coincident(g13,g5)
    c: Equal(g15,g12)
    c: Equal(g12,g9)
    c: DistanceY(g10,g10) = 2
    c: Equal(g10,g9)
FEATURE [PartDesign::Pad] Pad023
  Direction = (0,0,1)
  Length = 2
  Length2 = 10
  Profile = -> Sketch043
  ReferenceAxis = -> Sketch043 [N_Axis]
  Refine = true
  Suppressed = false
  Type = 0
  expr: Length = Spreadsheet.B1
FEATURE [PartDesign::Pad] Pad024
  BaseFeature = -> Pad023
  Direction = (0,0,1)
  Length = 7.1
  Length2 = 10
  Profile = -> Sketch044
  ReferenceAxis = -> Sketch044 [N_Axis]
  Refine = true
  Suppressed = false
  Type = 0
  expr: Length = Spreadsheet.B1 + Spreadsheet.B4 + Spreadsheet.B3
FEATURE [PartDesign::Fillet] Fillet010
  Base = -> Pad024 [Edge9,Edge3]
  BaseFeature = -> Pad024
  Radius = 5
  Refine = true
  SupportTransform = false
  Suppressed = false
  UseAllEdges = false
  expr: Radius = 5
FEATURE [Sketcher::SketchObject] Sketch045  label="border_tooth"
  ArcFitTolerance = 1e-06
  AttachmentOffset = pos=(0,0,7.1) rot=(0,0,1;0rad)
  AttachmentSupport = -> [XY_Plane003]
  ExternalGeometry = -> [Sketch043]
  FullyConstrained = true
  MakeInternals = false
  MapMode = 5
  Placement = pos=(0,0,7.1) rot=(0,0,1;0rad)
  expr: .AttachmentOffset.Base.z = Spreadsheet.B1 + Spreadsheet.B4 + Spreadsheet.B3
  sketch-geometry (16):
    g0: LineSegment StartX=-35.5 StartY=48.25 StartZ=0 EndX=-35.5 EndY=-70.75 EndZ=0
    g1: LineSegment StartX=-35.5 StartY=-70.75 StartZ=0 EndX=35.5 EndY=-70.75 EndZ=0
    g2: LineSegment StartX=35.5 StartY=-70.75 StartZ=0 EndX=35.5 EndY=48.25 EndZ=0
    g3: LineSegment StartX=35.5 StartY=48.25 StartZ=0 EndX=-35.5 EndY=48.25 EndZ=0
    g4: LineSegment StartX=-36.4 StartY=49.15 StartZ=0 EndX=-36.4 EndY=-71.65 EndZ=0
    g5: LineSegment StartX=-36.4 StartY=-71.65 StartZ=0 EndX=36.4 EndY=-71.65 EndZ=0
    g6: LineSegment StartX=36.4 StartY=-71.65 StartZ=0 EndX=36.4 EndY=49.15 EndZ=0
    g7: LineSegment StartX=36.4 StartY=49.15 StartZ=0 EndX=-36.4 EndY=49.15 EndZ=0
    g8: LineSegment [constr] StartX=-36.4 StartY=49.15 StartZ=0 EndX=-36.4 EndY=48.25 EndZ=0
    g9: LineSegment [constr] StartX=-36.4 StartY=48.25 StartZ=0 EndX=-35.5 EndY=48.25 EndZ=0
    g10: LineSegment [constr] StartX=-35.5 StartY=48.25 StartZ=0 EndX=-35.5 EndY=49.15 EndZ=0
    g11: LineSegment [constr] StartX=-35.5 StartY=49.15 StartZ=0 EndX=-36.4 EndY=49.15 EndZ=0
    g12: LineSegment [constr] StartX=35.5 StartY=-70.75 StartZ=0 EndX=35.5 EndY=-71.65 EndZ=0
    g13: LineSegment [constr] StartX=35.5 StartY=-71.65 StartZ=0 EndX=36.4 EndY=-71.65 EndZ=0
    g14: LineSegment [constr] StartX=36.4 StartY=-71.65 StartZ=0 EndX=36.4 EndY=-70.75 EndZ=0
    g15: LineSegment [constr] StartX=36.4 StartY=-70.75 StartZ=0 EndX=35.5 EndY=-70.75 EndZ=0
  constraints (42):
    c: Coincident(g0,g1)
    c: Coincident(g1,g2)
    c: Coincident(g2,g3)
    c: Coincident(g3,g0)
    c: Vertical(g0)
    c: Vertical(g2)
    c: Horizontal(g1)
    c: Horizontal(g3)
    c: Coincident(g0,g-4)
    c: Coincident(g1,g-6)
    c: Coincident(g4,g5)
    c: Coincident(g5,g6)
    c: Coincident(g6,g7)
    c: Coincident(g7,g4)
    c: Vertical(g4)
    c: Vertical(g6)
    c: Horizontal(g5)
    c: Horizontal(g7)
    c: Coincident(g8,g9)
    c: Coincident(g9,g10)
    c: Coincident(g10,g11)
    c: Coincident(g11,g8)
    c: Vertical(g8)
    c: Vertical(g10)
    c: Horizontal(g9)
    c: Horizontal(g11)
    c: Coincident(g8,g4)
    c: Coincident(g9,g0)
    c: Coincident(g12,g13)
    c: Coincident(g13,g14)
    c: Coincident(g14,g15)
    c: Coincident(g15,g12)
    c: Vertical(g12)
    c: Vertical(g14)
    c: Horizontal(g13)
    c: Horizontal(g15)
    c: Coincident(g12,g1)
    c: Coincident(g13,g5)
    c: Equal(g9,g10)
    c: Equal(g10,g15)
    c: Equal(g15,g12)
    c: DistanceX(g9,g9) = 0.9
FEATURE [PartDesign::Pad] Pad025
  BaseFeature = -> Fillet010
  Direction = (0,0,1)
  Length = 1.4
  Length2 = 10
  Profile = -> Sketch045
  ReferenceAxis = -> Sketch045 [N_Axis]
  Refine = true
  Suppressed = false
  Type = 0
FEATURE [PartDesign::SubShapeBinder] Binder003
  BindCopyOnChange = 0
  BindMode = 0
  ClaimChildren = false
  Context = -> Body003 [Binder003.]
  Fuse = false
  MakeFace = true
  OffsetFill = false
  OffsetIntersection = false
  OffsetJoinType = 0
  OffsetOpenResult = false
  PartialLoad = false
  Refine = true
  Relative = true
  Support = -> [Body002[Sketch040.]]
  _Version = 2
FEATURE [Sketcher::SketchObject] Sketch046  label="skrew_pads"
  ArcFitTolerance = 1e-06
  AttachmentSupport = -> [XY_Plane003]
  ExternalGeometry = -> [Binder002,Binder003]
  FullyConstrained = true
  MakeInternals = false
  MapMode = 5
  sketch-geometry (14):
    g0: Circle CenterX=-32.525 CenterY=45 CenterZ=0 NormalX=0 NormalY=0 NormalZ=1 AngleXU=0 Radius=2.25
    g1: Circle CenterX=32.525 CenterY=45 CenterZ=0 NormalX=0 NormalY=0 NormalZ=1 AngleXU=0 Radius=2.25
    g2: Circle CenterX=32.525 CenterY=-35 CenterZ=0 NormalX=0 NormalY=0 NormalZ=1 AngleXU=0 Radius=2.25
    g3: Circle CenterX=-32.525 CenterY=-45 CenterZ=0 NormalX=0 NormalY=0 NormalZ=1 AngleXU=0 Radius=2.25
    g4: Circle CenterX=-9.525 CenterY=-67.5 CenterZ=0 NormalX=0 NormalY=0 NormalZ=1 AngleXU=0 Radius=2.25
    g5: Circle CenterX=-32.525 CenterY=-67.5 CenterZ=0 NormalX=0 NormalY=0 NormalZ=1 AngleXU=0 Radius=2.25
    g6: Circle CenterX=-32.525 CenterY=45 CenterZ=0 NormalX=0 NormalY=0 NormalZ=1 AngleXU=0 Radius=1.25
    g7: LineSegment [constr] StartX=-32.525 StartY=45 StartZ=0 EndX=-30.275 EndY=45 EndZ=0
    g8: GeomPoint [constr] X=-31.275 Y=45 Z=0
    g9: Circle CenterX=32.525 CenterY=45 CenterZ=0 NormalX=0 NormalY=0 NormalZ=1 AngleXU=0 Radius=1.25
    g10: Circle CenterX=32.525 CenterY=-35 CenterZ=0 NormalX=0 NormalY=0 NormalZ=1 AngleXU=0 Radius=1.25
    g11: Circle CenterX=-32.525 CenterY=-45 CenterZ=0 NormalX=0 NormalY=0 NormalZ=1 AngleXU=0 Radius=1.25
    g12: Circle CenterX=-32.525 CenterY=-67.5 CenterZ=0 NormalX=0 NormalY=0 NormalZ=1 AngleXU=0 Radius=1.25
    g13: Circle CenterX=-9.525 CenterY=-67.5 CenterZ=0 NormalX=0 NormalY=0 NormalZ=1 AngleXU=0 Radius=1.25
  constraints (29):
    c: Coincident(g0,g-3)
    c: Equal(g0,g-3)
    c: Coincident(g1,g-4)
    c: Equal(g1,g-4)
    c: Coincident(g2,g-5)
    c: Equal(g2,g-5)
    c: Coincident(g3,g-8)
    c: Equal(g3,g-8)
    c: Coincident(g4,g-6)
    c: Equal(g4,g-6)
    c: Coincident(g5,g-7)
    c: Equal(g5,g-7)
    c: Coincident(g6,g0)
    c: Coincident(g7,g0)
    c: PointOnObject(g7,g0)
    c: Horizontal(g7)
    c: PointOnObject(g8,g6)
    c: PointOnObject(g8,g7)
    c: Distance(g8,g7) = 1
    c: Coincident(g9,g1)
    c: Coincident(g10,g2)
    c: Coincident(g11,g3)
    c: Coincident(g12,g5)
    c: Coincident(g13,g4)
    c: Equal(g11,g12)
    c: Equal(g12,g13)
    c: Equal(g9,g6)
    c: Equal(g10,g13)
    c: Equal(g10,g9)
FEATURE [Sketcher::SketchObject] Sketch047  label="skrew_holes_back"
  ArcFitTolerance = 1e-06
  AttachmentSupport = -> [XY_Plane003]
  ExternalGeometry = -> [Binder002,Binder003]
  FullyConstrained = true
  MakeInternals = false
  MapMode = 5
  expr: .AttachmentOffset.Base.z = 0
  sketch-geometry (6):
    g0: Circle CenterX=-32.525 CenterY=45 CenterZ=0 NormalX=0 NormalY=0 NormalZ=1 AngleXU=0 Radius=2.25
    g1: Circle CenterX=32.525 CenterY=45 CenterZ=0 NormalX=0 NormalY=0 NormalZ=1 AngleXU=0 Radius=2.25
    g2: Circle CenterX=32.525 CenterY=-35 CenterZ=0 NormalX=0 NormalY=0 NormalZ=1 AngleXU=0 Radius=2.25
    g3: Circle CenterX=-9.525 CenterY=-67.5 CenterZ=0 NormalX=0 NormalY=0 NormalZ=1 AngleXU=0 Radius=2.25
    g4: Circle CenterX=-32.525 CenterY=-67.5 CenterZ=0 NormalX=0 NormalY=0 NormalZ=1 AngleXU=0 Radius=2.25
    g5: Circle CenterX=-32.525 CenterY=-45 CenterZ=0 NormalX=0 NormalY=0 NormalZ=1 AngleXU=0 Radius=2.25
  constraints (12):
    c: Coincident(g0,g-3)
    c: Coincident(g1,g-4)
    c: Coincident(g2,g-5)
    c: Coincident(g3,g-6)
    c: Coincident(g4,g-7)
    c: Coincident(g5,g-8)
    c: Equal(g0,g1)
    c: Equal(g2,g5)
    c: Equal(g5,g4)
    c: Equal(g4,g3)
    c: Diameter(g0) = 4.5
    c: Equal(g2,g1)
FEATURE [Sketcher::SketchObject] Sketch048
  ArcFitTolerance = 1e-06
  AttachmentOffset = pos=(0,0,4.5) rot=(0,0,1;0rad)
  AttachmentSupport = -> [XY_Plane003]
  ExternalGeometry = -> [Sketch047]
  FullyConstrained = true
  MakeInternals = false
  MapMode = 5
  Placement = pos=(0,0,4.5) rot=(0,0,1;0rad)
  expr: .AttachmentOffset.Base.z = Spreadsheet.B1 + 2.5
  sketch-geometry (6):
    g0: Circle CenterX=-32.525 CenterY=45 CenterZ=0 NormalX=0 NormalY=0 NormalZ=1 AngleXU=0 Radius=2.25
    g1: Circle CenterX=32.525 CenterY=45 CenterZ=0 NormalX=0 NormalY=0 NormalZ=1 AngleXU=0 Radius=2.25
    g2: Circle CenterX=32.525 CenterY=-35 CenterZ=0 NormalX=0 NormalY=0 NormalZ=1 AngleXU=0 Radius=2.25
    g3: Circle CenterX=-9.525 CenterY=-67.5 CenterZ=0 NormalX=0 NormalY=0 NormalZ=1 AngleXU=0 Radius=2.25
    g4: Circle CenterX=-32.525 CenterY=-67.5 CenterZ=0 NormalX=0 NormalY=0 NormalZ=1 AngleXU=0 Radius=2.25
    g5: Circle CenterX=-32.525 CenterY=-45 CenterZ=0 NormalX=0 NormalY=0 NormalZ=1 AngleXU=0 Radius=2.25
  constraints (12):
    c: Equal(g0,g1)
    c: Equal(g2,g3)
    c: Equal(g3,g4)
    c: Equal(g2,g1)
    c: Equal(g5,g2)
    c: Coincident(g5,g-5)
    c: Coincident(g4,g-6)
    c: Coincident(g3,g-7)
    c: Coincident(g0,g-3)
    c: Coincident(g1,g-4)
    c: Coincident(g2,g-8)
    c: Equal(g1,g-4)
FEATURE [Sketcher::SketchObject] Sketch049
  ArcFitTolerance = 1e-06
  AttachmentSupport = -> [XY_Plane003]
  FullyConstrained = true
  MakeInternals = false
  MapMode = 5
  sketch-geometry (6):
    g0: Circle CenterX=-32.525 CenterY=45 CenterZ=0 NormalX=0 NormalY=0 NormalZ=1 AngleXU=0 Radius=1.3
    g1: Circle CenterX=32.525 CenterY=45 CenterZ=0 NormalX=0 NormalY=0 NormalZ=1 AngleXU=0 Radius=1.3
    g2: Circle CenterX=-32.525 CenterY=-67.5 CenterZ=0 NormalX=0 NormalY=0 NormalZ=1 AngleXU=0 Radius=1.3
    g3: Circle CenterX=-32.525 CenterY=-45 CenterZ=0 NormalX=0 NormalY=0 NormalZ=1 AngleXU=0 Radius=1.3
    g4: Circle CenterX=-9.525 CenterY=-67.5 CenterZ=0 NormalX=0 NormalY=0 NormalZ=1 AngleXU=0 Radius=1.3
    g5: Circle CenterX=32.525 CenterY=-35 CenterZ=0 NormalX=0 NormalY=0 NormalZ=1 AngleXU=0 Radius=1.3
  constraints (12):
    c: Coincident(g0,g-3)
    c: Coincident(g1,g-4)
    c: Coincident(g2,g-7)
    c: Coincident(g3,g-5)
    c: Coincident(g4,g-8)
    c: Coincident(g5,g-6)
    c: Equal(g0,g1)
    c: Equal(g5,g4)
    c: Equal(g4,g2)
    c: Equal(g2,g3)
    c: Equal(g-4,g1)
    c: Equal(g5,g0)
FEATURE [Sketcher::SketchObject] Sketch050  label="usb_c_hole"
  ArcFitTolerance = 1e-06
  AttachmentOffset = pos=(0,0,-35.5) rot=(0,0,1;0rad)
  AttachmentSupport = -> [YZ_Plane003]
  ExternalGeometry = -> [Binder002]
  FullyConstrained = true
  MakeInternals = false
  MapMode = 5
  Placement = pos=(-35.5,0,0) rot=(0.57735,0.57735,0.57735;2.0944rad)
  expr: Constraints[15] = Spreadsheet.B1 + Spreadsheet.B4
  sketch-geometry (7):
    g0: ArcOfCircle CenterX=33.5 CenterY=3.9 CenterZ=0 NormalX=0 NormalY=0 NormalZ=1 AngleXU=0 Radius=1.6 StartAngle=1.5708 EndAngle=4.71239
    g1: ArcOfCircle CenterX=39.5 CenterY=3.9 CenterZ=0 NormalX=0 NormalY=0 NormalZ=1 AngleXU=0 Radius=1.6 StartAngle=4.71239 EndAngle=7.85398
    g2: LineSegment StartX=33.5 StartY=5.5 StartZ=0 EndX=39.5 EndY=5.5 EndZ=0
    g3: LineSegment StartX=33.5 StartY=2.3 StartZ=0 EndX=39.5 EndY=2.3 EndZ=0
    g4: LineSegment [constr] StartX=33.5 StartY=3.9 StartZ=0 EndX=39.5 EndY=3.9 EndZ=0
    g5: Circle [constr] CenterX=45 CenterY=-2 CenterZ=0 NormalX=0 NormalY=0 NormalZ=1 AngleXU=0 Radius=0.95
    g6: Circle [constr] CenterX=36.5 CenterY=3.9 CenterZ=0 NormalX=0 NormalY=0 NormalZ=1 AngleXU=0 Radius=3
  constraints (16):
    c: Tangent(g0,g2) = 1.5708
    c: Tangent(g0,g3) = -1.5708
    c: Tangent(g1,g2) = 1.5708
    c: Tangent(g1,g3) = -1.5708
    c: Equal(g0,g1)
    c: Horizontal(g3)
    c: DistanceY(g1,g1) = 3.2
    c: Coincident(g4,g0)
    c: Coincident(g4,g1)
    c: DistanceX(g4,g4) = 6
    c: Symmetric(g-3,g-3,g5)
    c: PointOnObject(g-3,g5)
    c: Symmetric(g4,g4,g6)
    c: PointOnObject(g1,g6)
    c: DistanceX(g6,g5) = 8.5
    c: DistanceY(g-1,g1) = 5.5
FEATURE [Sketcher::SketchObject] Sketch051  label="sd_hole"
  ArcFitTolerance = 1e-06
  AttachmentOffset = pos=(0,0,-35.5) rot=(0,0,1;0rad)
  AttachmentSupport = -> [YZ_Plane003]
  ExternalGeometry = -> [Binder002]
  FullyConstrained = true
  MakeInternals = false
  MapMode = 5
  Placement = pos=(-35.5,0,0) rot=(0.57735,0.57735,0.57735;2.0944rad)
  expr: Constraints[13] = Spreadsheet.B1 + Spreadsheet.B4 - 0.5
  sketch-geometry (5):
    g0: LineSegment StartX=-27.5 StartY=5 StartZ=0 EndX=-27.5 EndY=3 EndZ=0
    g1: LineSegment StartX=-27.5 StartY=3 StartZ=0 EndX=-15.5 EndY=3 EndZ=0
    g2: LineSegment StartX=-15.5 StartY=3 StartZ=0 EndX=-15.5 EndY=5 EndZ=0
    g3: LineSegment StartX=-15.5 StartY=5 StartZ=0 EndX=-27.5 EndY=5 EndZ=0
    g4: Circle [constr] CenterX=-45 CenterY=-2 CenterZ=0 NormalX=0 NormalY=0 NormalZ=1 AngleXU=0 Radius=0.95
  constraints (14):
    c: Coincident(g0,g1)
    c: Coincident(g1,g2)
    c: Coincident(g2,g3)
    c: Coincident(g3,g0)
    c: Vertical(g0)
    c: Vertical(g2)
    c: Horizontal(g1)
    c: Horizontal(g3)
    c: DistanceX(g3,g3) = 12
    c: DistanceY(g0,g0) = 2
    c: Symmetric(g-3,g-3,g4)
    c: PointOnObject(g-3,g4)
    c: DistanceX(g4,g0) = 17.5
    c: DistanceY(g-1,g0) = 5
FEATURE [Sketcher::SketchObject] Sketch052  label="switch_hole"
  ArcFitTolerance = 1e-06
  AttachmentOffset = pos=(0,0,38) rot=(0,0,1;0rad)
  AttachmentSupport = -> [YZ_Plane003]
  ExternalGeometry = -> [Binder002]
  FullyConstrained = true
  MakeInternals = false
  MapMode = 5
  Placement = pos=(38,0,0) rot=(0.57735,0.57735,0.57735;2.0944rad)
  expr: Constraints[16] = Spreadsheet.B1 + Spreadsheet.B4 - 0.9
  sketch-geometry (8):
    g0: LineSegment StartX=-5 StartY=6.6 StartZ=0 EndX=-5 EndY=2.6 EndZ=0
    g1: LineSegment StartX=-5 StartY=2.6 StartZ=0 EndX=9.5 EndY=2.6 EndZ=0
    g2: LineSegment StartX=9.5 StartY=2.6 StartZ=0 EndX=9.5 EndY=6.6 EndZ=0
    g3: LineSegment StartX=9.5 StartY=6.6 StartZ=0 EndX=-5 EndY=6.6 EndZ=0
    g4: LineSegment [constr] StartX=-5 StartY=6.6 StartZ=0 EndX=9.5 EndY=2.6 EndZ=0
    g5: LineSegment [constr] StartX=9.5 StartY=6.6 StartZ=0 EndX=-5 EndY=2.6 EndZ=0
    g6: GeomPoint [constr] X=2.25 Y=4.6 Z=0
    g7: Circle [constr] CenterX=-35 CenterY=-2 CenterZ=0 NormalX=0 NormalY=0 NormalZ=1 AngleXU=0 Radius=0.95
  constraints (20):
    c: Coincident(g0,g1)
    c: Coincident(g1,g2)
    c: Coincident(g2,g3)
    c: Coincident(g3,g0)
    c: Vertical(g0)
    c: Vertical(g2)
    c: Horizontal(g1)
    c: Horizontal(g3)
    c: DistanceX(g3,g3) = 14.5
    c: DistanceY(g2,g2) = 4
    c: Coincident(g4,g0)
    c: Coincident(g4,g1)
    c: Coincident(g5,g2)
    c: Coincident(g5,g0)
    c: PointOnObject(g6,g4)
    c: PointOnObject(g6,g5)
    c: DistanceY(g-1,g6) = 4.6
    c: Symmetric(g-3,g-3,g7)
    c: PointOnObject(g-3,g7)
    c: DistanceX(g7,g6) = 37.25
FEATURE [PartDesign::Pocket] Pocket019
  BaseFeature = -> Pad025
  Direction = (-1,0,0)
  Length = 5
  Length2 = 5
  Profile = -> Sketch052
  ReferenceAxis = -> Sketch052 [N_Axis]
  Refine = true
  Suppressed = false
  Type = 0
FEATURE [Sketcher::SketchObject] Sketch053  label="usb_c_hole_big"
  ArcFitTolerance = 1e-06
  AttachmentOffset = pos=(0,0,2) rot=(0,0,1;0rad)
  AttachmentSupport = -> [XY_Plane003]
  ExternalGeometry = -> [Sketch050]
  FullyConstrained = true
  MakeInternals = false
  MapMode = 5
  Placement = pos=(0,0,2) rot=(0,0,1;0rad)
  expr: .AttachmentOffset.Base.z = Spreadsheet.B1
  sketch-geometry (8):
    g0: LineSegment StartX=-36.25 StartY=41.5 StartZ=0 EndX=-36.25 EndY=31.5 EndZ=0
    g1: LineSegment StartX=-36.25 StartY=31.5 StartZ=0 EndX=-34.75 EndY=31.5 EndZ=0
    g2: LineSegment StartX=-34.75 StartY=31.5 StartZ=0 EndX=-34.75 EndY=41.5 EndZ=0
    g3: LineSegment StartX=-34.75 StartY=41.5 StartZ=0 EndX=-36.25 EndY=41.5 EndZ=0
    g4: LineSegment [constr] StartX=-36.25 StartY=41.5 StartZ=0 EndX=-34.75 EndY=31.5 EndZ=0
    g5: LineSegment [constr] StartX=-34.75 StartY=41.5 StartZ=0 EndX=-36.25 EndY=31.5 EndZ=0
    g6: Circle [constr] CenterX=-35.5 CenterY=36.5 CenterZ=0 NormalX=0 NormalY=0 NormalZ=1 AngleXU=0 Radius=3
    g7: GeomPoint [constr] X=-35.5 Y=36.5 Z=0
  constraints (20):
    c: Coincident(g0,g1)
    c: Coincident(g1,g2)
    c: Coincident(g2,g3)
    c: Coincident(g3,g0)
    c: Vertical(g0)
    c: Vertical(g2)
    c: Horizontal(g1)
    c: Horizontal(g3)
    c: Coincident(g4,g0)
    c: Coincident(g4,g1)
    c: Coincident(g5,g2)
    c: Coincident(g5,g0)
    c: PointOnObject(g6,g-3)
    c: PointOnObject(g-3,g6)
    c: PointOnObject(g-3,g6)
    c: PointOnObject(g7,g4)
    c: PointOnObject(g7,g5)
    c: Coincident(g7,g6)
    c: DistanceY(g2,g2) = 10
    c: DistanceX(g3,g3) = 1.5
FEATURE [PartDesign::Pocket] Pocket020
  BaseFeature = -> Pocket019
  Direction = (0,0,-1)
  Length = 10
  Length2 = 5
  Profile = -> Sketch053
  ReferenceAxis = -> Sketch053 [N_Axis]
  Refine = true
  Reversed = true
  Suppressed = false
  Type = 0
FEATURE [PartDesign::Pocket] Pocket021
  BaseFeature = -> Pocket020
  Direction = (-1,0,0)
  Length = 5
  Length2 = 5
  Profile = -> Sketch050
  ReferenceAxis = -> Sketch050 [N_Axis]
  Refine = true
  Suppressed = false
  Type = 0
FEATURE [PartDesign::Pocket] Pocket022
  BaseFeature = -> Pocket021
  Direction = (-1,0,0)
  Length = 5
  Length2 = 5
  Profile = -> Sketch051
  ReferenceAxis = -> Sketch051 [N_Axis]
  Refine = true
  Suppressed = false
  Type = 0
FEATURE [Sketcher::SketchObject] Sketch054  label="gpio_hole"
  ArcFitTolerance = 1e-06
  AttachmentOffset = pos=(0,0,-51) rot=(0,0,1;0rad)
  AttachmentSupport = -> [XZ_Plane002]
  ExternalGeometry = -> [Sketch021]
  FullyConstrained = true
  MakeInternals = false
  MapMode = 5
  Placement = pos=(0,51,-1.13e-14) rot=(1,0,0;1.5708rad)
  sketch-geometry (5):
    g0: LineSegment StartX=-21.725 StartY=-4.7 StartZ=0 EndX=-21.725 EndY=-7.5 EndZ=0
    g1: LineSegment StartX=-21.725 StartY=-7.5 StartZ=0 EndX=4.775 EndY=-7.5 EndZ=0
    g2: LineSegment StartX=4.775 StartY=-7.5 StartZ=0 EndX=4.775 EndY=-4.7 EndZ=0
    g3: LineSegment StartX=4.775 StartY=-4.7 StartZ=0 EndX=-21.725 EndY=-4.7 EndZ=0
    g4: Circle [constr] CenterX=-32.525 CenterY=-2 CenterZ=0 NormalX=0 NormalY=0 NormalZ=1 AngleXU=0 Radius=2.25
  constraints (14):
    c: Coincident(g0,g1)
    c: Coincident(g1,g2)
    c: Coincident(g2,g3)
    c: Coincident(g3,g0)
    c: Vertical(g0)
    c: Vertical(g2)
    c: Horizontal(g1)
    c: Horizontal(g3)
    c: Distance(g0,g2) = 26.5
    c: Distance(g1,g3) = 2.8
    c: DistanceY(g1,g-1) = 7.5
    c: Symmetric(g-3,g-3,g4)
    c: PointOnObject(g-3,g4)
    c: DistanceX(g4,g0) = 10.8
FEATURE [PartDesign::Pocket] Pocket023
  BaseFeature = -> Fillet009
  Direction = (0,1,-2e-16)
  Length = 5
  Length2 = 5
  Profile = -> Sketch054
  ReferenceAxis = -> Sketch054 [N_Axis]
  Refine = true
  Reversed = true
  Suppressed = false
  Type = 0
FEATURE [PartDesign::SubShapeBinder] Binder004
  BindCopyOnChange = 0
  BindMode = 0
  ClaimChildren = false
  Context = -> Body003 [Binder004.]
  Fuse = false
  MakeFace = true
  OffsetFill = false
  OffsetIntersection = false
  OffsetJoinType = 0
  OffsetOpenResult = false
  PartialLoad = false
  Refine = true
  Relative = true
  Support = -> [Body002[Sketch054.]]
  _Version = 2
FEATURE [Sketcher::SketchObject] Sketch055  label="gpio_hole001"
  ArcFitTolerance = 1e-06
  AttachmentOffset = pos=(0,0,-51) rot=(0,0,1;0rad)
  AttachmentSupport = -> [XZ_Plane003]
  ExternalGeometry = -> [Binder004]
  FullyConstrained = true
  MakeInternals = false
  MapMode = 5
  Placement = pos=(0,51,-1.13e-14) rot=(1,0,0;1.5708rad)
  expr: Constraints[23] = Spreadsheet.B1 + Spreadsheet.B4 + Spreadsheet.B3
  sketch-geometry (9):
    g0: LineSegment [constr] StartX=-21.725 StartY=-4.7 StartZ=0 EndX=-21.725 EndY=-7.5 EndZ=0
    g1: LineSegment [constr] StartX=-21.725 StartY=-7.5 StartZ=0 EndX=4.775 EndY=-7.5 EndZ=0
    g2: LineSegment [constr] StartX=4.775 StartY=-7.5 StartZ=0 EndX=4.775 EndY=-4.7 EndZ=0
    g3: LineSegment [constr] StartX=4.775 StartY=-4.7 StartZ=0 EndX=-21.725 EndY=-4.7 EndZ=0
    g4: LineSegment StartX=-21.725 StartY=9.9 StartZ=0 EndX=-21.725 EndY=7.1 EndZ=0
    g5: LineSegment StartX=-21.725 StartY=7.1 StartZ=0 EndX=4.775 EndY=7.1 EndZ=0
    g6: LineSegment StartX=4.775 StartY=7.1 StartZ=0 EndX=4.775 EndY=9.9 EndZ=0
    g7: LineSegment StartX=4.775 StartY=9.9 StartZ=0 EndX=-21.725 EndY=9.9 EndZ=0
    g8: LineSegment [constr] StartX=-21.725 StartY=7.1 StartZ=0 EndX=-21.725 EndY=-4.7 EndZ=0
  constraints (24):
    c: Coincident(g0,g1)
    c: Coincident(g1,g2)
    c: Coincident(g2,g3)
    c: Coincident(g3,g0)
    c: Vertical(g0)
    c: Vertical(g2)
    c: Horizontal(g1)
    c: Horizontal(g3)
    c: Coincident(g0,g-3)
    c: Coincident(g1,g-4)
    c: Coincident(g4,g5)
    c: Coincident(g5,g6)
    c: Coincident(g6,g7)
    c: Coincident(g7,g4)
    c: Vertical(g4)
    c: Vertical(g6)
    c: Horizontal(g5)
    c: Horizontal(g7)
    c: Equal(g5,g3)
    c: Equal(g6,g2)
    c: Coincident(g8,g4)
    c: Coincident(g8,g0)
    c: Vertical(g8)
    c: DistanceY(g-1,g5) = 7.1
FEATURE [PartDesign::Pocket] Pocket024
  BaseFeature = -> Pocket022
  Direction = (0,1,-2e-16)
  Length = 5
  Length2 = 5
  Profile = -> Sketch055
  ReferenceAxis = -> Sketch055 [N_Axis]
  Refine = true
  Reversed = true
  Suppressed = false
  Type = 0
FEATURE [PartDesign::Fillet] Fillet014
  Base = -> Pocket024 [Edge59,Edge65]
  BaseFeature = -> Pocket024
  Radius = 2
  Refine = true
  SupportTransform = false
  Suppressed = false
  UseAllEdges = false
  expr: Radius = Spreadsheet.B1
FEATURE [PartDesign::Fillet] Fillet017
  Base = -> Pocket023 [Edge424,Edge425,Edge423,Edge426,Edge428,Edge429,Edge427,Edge430,Edge433,Edge434,Edge435,Edge436,Edge437,Edge440,Edge438,Edge439]
  BaseFeature = -> Pocket023
  Radius = 1
  Refine = true
  SupportTransform = false
  Suppressed = false
  UseAllEdges = false
FEATURE [Sketcher::SketchObject] Sketch056  label="skrew_pads_fat"
  ArcFitTolerance = 1e-06
  AttachmentOffset = pos=(0,0,2) rot=(0,0,1;0rad)
  AttachmentSupport = -> [XY_Plane003]
  ExternalGeometry = -> [Sketch048]
  FullyConstrained = true
  MakeInternals = false
  MapMode = 5
  Placement = pos=(0,0,2) rot=(0,0,1;0rad)
  expr: .AttachmentOffset.Base.z = Spreadsheet.B1
  sketch-geometry (6):
    g0: Circle CenterX=-32.525 CenterY=45 CenterZ=0 NormalX=0 NormalY=0 NormalZ=1 AngleXU=0 Radius=3.25
    g1: Circle CenterX=32.525 CenterY=45 CenterZ=0 NormalX=0 NormalY=0 NormalZ=1 AngleXU=0 Radius=3.25
    g2: Circle CenterX=32.525 CenterY=-35 CenterZ=0 NormalX=0 NormalY=0 NormalZ=1 AngleXU=0 Radius=3.25
    g3: Circle CenterX=-9.525 CenterY=-67.5 CenterZ=0 NormalX=0 NormalY=0 NormalZ=1 AngleXU=0 Radius=3.25
    g4: Circle CenterX=-32.525 CenterY=-67.5 CenterZ=0 NormalX=0 NormalY=0 NormalZ=1 AngleXU=0 Radius=3.25
    g5: Circle CenterX=-32.525 CenterY=-45 CenterZ=0 NormalX=0 NormalY=0 NormalZ=1 AngleXU=0 Radius=3.25
  constraints (12):
    c: Coincident(g0,g-3)
    c: Coincident(g1,g-4)
    c: Coincident(g2,g-8)
    c: Coincident(g3,g-7)
    c: Coincident(g4,g-6)
    c: Coincident(g5,g-5)
    c: Equal(g0,g1)
    c: Equal(g1,g2)
    c: Equal(g2,g5)
    c: Equal(g5,g4)
    c: Equal(g4,g3)
    c: Diameter(g0) = 6.5
FEATURE [PartDesign::Pad] Pad026
  BaseFeature = -> Fillet014
  Direction = (0,0,1)
  Length = 2.5
  Length2 = 10
  Profile = -> Sketch056
  ReferenceAxis = -> Sketch056 [N_Axis]
  Refine = true
  Suppressed = false
  Type = 0
FEATURE [PartDesign::Pad] Pad027
  BaseFeature = -> Pad026
  Direction = (0,0,1)
  Length = 0.9
  Length2 = 10
  Profile = -> Sketch048
  ReferenceAxis = -> Sketch048 [N_Axis]
  Refine = true
  Suppressed = false
  Type = 0
FEATURE [Sketcher::SketchObject] Sketch057  label="skrew_holes"
  ArcFitTolerance = 1e-06
  AttachmentSupport = -> [XY_Plane003]
  ExternalGeometry = -> [Sketch049]
  FullyConstrained = true
  MakeInternals = false
  MapMode = 5
  sketch-geometry (6):
    g0: Circle CenterX=-32.525 CenterY=45 CenterZ=0 NormalX=0 NormalY=0 NormalZ=1 AngleXU=0 Radius=1.25
    g1: Circle CenterX=32.525 CenterY=45 CenterZ=0 NormalX=0 NormalY=0 NormalZ=1 AngleXU=0 Radius=1.25
    g2: Circle CenterX=-32.525 CenterY=-45 CenterZ=0 NormalX=0 NormalY=0 NormalZ=1 AngleXU=0 Radius=1.25
    g3: Circle CenterX=-32.525 CenterY=-67.5 CenterZ=0 NormalX=0 NormalY=0 NormalZ=1 AngleXU=0 Radius=1.25
    g4: Circle CenterX=-9.525 CenterY=-67.5 CenterZ=0 NormalX=0 NormalY=0 NormalZ=1 AngleXU=0 Radius=1.25
    g5: Circle CenterX=32.525 CenterY=-35 CenterZ=0 NormalX=0 NormalY=0 NormalZ=1 AngleXU=0 Radius=1.25
  constraints (12):
    c: Coincident(g0,g-3)
    c: Coincident(g1,g-4)
    c: Coincident(g2,g-5)
    c: Coincident(g3,g-6)
    c: Coincident(g4,g-7)
    c: Coincident(g5,g-8)
    c: Equal(g0,g1)
    c: Equal(g1,g5)
    c: Equal(g5,g2)
    c: Equal(g2,g3)
    c: Equal(g3,g4)
    c: Diameter(g0) = 2.5
FEATURE [PartDesign::Pocket] Pocket025
  BaseFeature = -> Pad027
  Direction = (0,0,-1)
  Length = 5.5
  Length2 = 5
  Profile = -> Sketch057
  ReferenceAxis = -> Sketch057 [N_Axis]
  Refine = true
  Reversed = true
  Suppressed = false
  Type = 0
  expr: Length = Spreadsheet.B4 + Spreadsheet.B1
FEATURE [PartDesign::Fillet] Fillet018
  Base = -> Pocket025 [Edge184,Edge183,Edge181,Edge182]
  BaseFeature = -> Pocket025
  Radius = 1.2
  Refine = true
  SupportTransform = false
  Suppressed = false
  UseAllEdges = false
FEATURE [PartDesign::Fillet] Fillet019
  Base = -> Fillet018 [Edge150]
  BaseFeature = -> Fillet018
  Radius = 0.85
  Refine = true
  SupportTransform = false
  Suppressed = false
  UseAllEdges = false
FEATURE [PartDesign::Pocket] Pocket026
  BaseFeature = -> Fillet019
  Direction = (0,0,-1)
  Length = 3
  Length2 = 5
  Profile = -> Sketch047
  ReferenceAxis = -> Sketch047 [N_Axis]
  Refine = true
  Reversed = true
  Suppressed = false
  Type = 0
FEATURE [PartDesign::Fillet] Fillet020
  Base = -> Pocket026 [Edge246,Edge72,Edge67,Edge237,Edge236,Edge245]
  BaseFeature = -> Pocket026
  Radius = 0.4
  Refine = true
  SupportTransform = false
  Suppressed = false
  UseAllEdges = false
FEATURE [PartDesign::Fillet] Fillet022
  Base = -> Fillet017 [Edge49,Edge53,Edge51,Edge52,Edge50,Edge54,Edge56,Edge58,Edge60,Edge59,Edge57,Edge55,Edge63,Edge64]
  BaseFeature = -> Fillet017
  Radius = 0.5
  Refine = true
  SupportTransform = false
  Suppressed = false
  UseAllEdges = false
FEATURE [PartDesign::Fillet] Fillet023
  Base = -> Fillet022 [Edge497,Edge496,Edge516,Edge450,Edge479,Edge484,Edge483,Edge480]
  BaseFeature = -> Fillet022
  Radius = 1
  Refine = true
  SupportTransform = false
  Suppressed = false
  UseAllEdges = false
FEATURE [PartDesign::Body] Body002  label="front"
  AllowCompound = false
  Group = -> [Sketch021,Sketch022,Sketch023,Pad011,Pad012,Fillet004,Pad013,Fillet005,Sketch024,Pocket008,Sketch025,Pad014,Sketch026,Pad015,Sketch027,Sketch028,Pad016,Sketch029,Pad017,Sketch030,Pad018,Fillet007,Pocket009,Sketch031,Pocket010,Sketch032,Pad019,Sketch033,Pad020,Sketch034,Sketch036,Sketch037,Sketch038,Pocket011,PolarPattern,Pocket012,PolarPattern001,Pocket013,PolarPattern002,Sketch039,Pad021,+12 more]
  Origin = -> Origin002
  Tip = -> Fillet023
FEATURE [PartDesign::SubShapeBinder] Binder005
  BindCopyOnChange = 0
  BindMode = 0
  ClaimChildren = false
  Context = -> Body003 [Binder005.]
  Fuse = false
  MakeFace = true
  OffsetFill = false
  OffsetIntersection = false
  OffsetJoinType = 0
  OffsetOpenResult = false
  PartialLoad = false
  Refine = true
  Relative = true
  Support = -> [Body002[Sketch039.]]
  _Version = 2
FEATURE [PartDesign::SubShapeBinder] Binder
  BindCopyOnChange = 0
  BindMode = 0
  ClaimChildren = false
  Context = -> Body003 [Binder.]
  Fuse = false
  MakeFace = true
  OffsetFill = false
  OffsetIntersection = false
  OffsetJoinType = 0
  OffsetOpenResult = false
  PartialLoad = false
  Refine = true
  Relative = true
  Support = -> [Body002[Sketch033.]]
  _Version = 2
FEATURE [Sketcher::SketchObject] Sketch  label="speaker_holder"
  ArcFitTolerance = 1e-06
  AttachmentSupport = -> [XY_Plane003]
  ExternalGeometry = -> [Binder]
  FullyConstrained = true
  MakeInternals = false
  MapMode = 5
  sketch-geometry (2):
    g0: Circle CenterX=-20.6756 CenterY=-58.3228 CenterZ=0 NormalX=0 NormalY=0 NormalZ=1 AngleXU=0 Radius=5
    g1: Circle CenterX=-20.6756 CenterY=-58.3228 CenterZ=0 NormalX=0 NormalY=0 NormalZ=1 AngleXU=0 Radius=3
  constraints (4):
    c: Coincident(g0,g-3)
    c: Coincident(g1,g0)
    c: Diameter(g0) = 10
    c: Diameter(g1) = 6
FEATURE [PartDesign::Pad] Pad
  BaseFeature = -> Fillet020
  Direction = (0,0,1)
  Length = 5
  Length2 = 10
  Profile = -> Sketch
  ReferenceAxis = -> Sketch [N_Axis]
  Refine = true
  Suppressed = false
  Type = 0
  expr: Length = Spreadsheet.B1 + 3
FEATURE [PartDesign::Fillet] Fillet
  Base = -> Pad [Edge185,Edge186,Edge194,Edge193]
  BaseFeature = -> Pad
  Radius = 1
  Refine = true
  SupportTransform = false
  Suppressed = false
  UseAllEdges = false
FEATURE [PartDesign::Body] Body003  label="back"
  AllowCompound = false
  Group = -> [Binder001,Binder002,Sketch043,Sketch044,Pad023,Pad024,Fillet010,Sketch045,Pad025,Binder003,Sketch046,Sketch047,Sketch048,Sketch049,Sketch050,Sketch051,Sketch052,Pocket019,Sketch053,Pocket020,Pocket021,Pocket022,Binder004,Sketch055,Pocket024,Fillet014,Sketch056,Pad026,Pad027,Sketch057,Pocket025,Fillet018,Fillet019,Pocket026,Fillet020,Binder005,Binder,Sketch,Pad,Fillet]
  Origin = -> Origin003
  Tip = -> Fillet
FEATURE [Measure::MeasureDistance] Distance  label="Distance: 0.50 mm"
  Distance = 0.5
  DistanceX = 0
  DistanceY = 1.8e-15
  DistanceZ = 0.5
  Element1 = -> Body003 [Fillet.Edge109]
  Element2 = -> Body003 [Fillet.Edge33]
  Position1 = (37.5,-5,7.1)
  Position2 = (37.5,-5,6.6)
FEATURE [Measure::MeasureLength] Length  label="Length: 1.20 mm"
  Elements = -> [Body002]
  Length = 1.2
FEATURE [Measure::MeasureLength] Length001  label="Length001: 0.80 mm"
  Elements = -> [Body002]
  Length = 0.8
FEATURE [Measure::MeasureLength] Length002  label="Length002: 2.80 mm"
  Elements = -> [Body002]
  Length = 2.8
FEATURE [App::DocumentObjectGroup] Measurements
  Group = -> [Distance,Length,Length001,Length002]
FEATURE [Part::Part2DObjectPython] ShapeString  label="menu_ss"  # Draft 2D object (typed FeaturePython)
  FontFile = BarlowCondensed-SemiBold.ttf
  Fuse = false
  Justification = 6
  JustificationReference = 0
  KeepLeftMargin = false
  MakeFace = true
  ObliqueAngle = 0
  Placement = pos=(-26.8,-18.5,0) rot=(0,0,1;0rad)
  ScaleToSize = true
  Size = 2.5
  String = MENU
  Tracking = 0
FEATURE [Part::Part2DObjectPython] ShapeString001  label="volume_ss"  # Draft 2D object (typed FeaturePython)
  FontFile = BarlowCondensed-SemiBold.ttf
  Fuse = false
  Justification = 6
  JustificationReference = 0
  KeepLeftMargin = false
  MakeFace = true
  ObliqueAngle = 0
  Placement = pos=(-16.9,-18.5,0) rot=(0,0,1;0rad)
  ScaleToSize = true
  Size = 2.5
  String = VOLUME
  Tracking = 0
FEATURE [Part::Part2DObjectPython] ShapeString002  label="start_ss"  # Draft 2D object (typed FeaturePython)
  FontFile = BarlowCondensed-SemiBold.ttf
  Fuse = false
  Justification = 6
  JustificationReference = 0
  KeepLeftMargin = false
  MakeFace = true
  ObliqueAngle = 0
  Placement = pos=(19.6,-18.5,0) rot=(0,0,1;0rad)
  ScaleToSize = true
  Size = 2.5
  String = START
  Tracking = 0
FEATURE [Part::Part2DObjectPython] ShapeString003  label="select_ss"  # Draft 2D object (typed FeaturePython)
  FontFile = BarlowCondensed-SemiBold.ttf
  Fuse = false
  Justification = 6
  JustificationReference = 0
  KeepLeftMargin = false
  MakeFace = true
  ObliqueAngle = 0
  Placement = pos=(7.5,-18.5,0) rot=(0,0,1;0rad)
  ScaleToSize = true
  Size = 2.5
  String = SELECT
  Tracking = 0
FEATURE [Part::Extrusion] Extrude  label="menu_e"
  Base = -> ShapeString
  Dir = (0,0,1)
  DirMode = 0
  FaceMakerClass = Part::FaceMakerBullseye
  FaceMakerMode = 3
  LengthFwd = 0.5
  LengthRev = 0
  Solid = false
  Symmetric = false
FEATURE [Part::Extrusion] Extrude001  label="volume_e"
  Base = -> ShapeString001
  Dir = (0,0,1)
  DirMode = 0
  FaceMakerClass = Part::FaceMakerBullseye
  FaceMakerMode = 3
  LengthFwd = 0.5
  LengthRev = 0
  Solid = false
  Symmetric = false
FEATURE [Part::Extrusion] Extrude003  label="select_e"
  Base = -> ShapeString003
  Dir = (0,0,1)
  DirMode = 0
  FaceMakerClass = Part::FaceMakerBullseye
  FaceMakerMode = 3
  LengthFwd = 0.5
  LengthRev = 0
  Solid = false
  Symmetric = false
FEATURE [Part::Extrusion] Extrude004  label="start_e"
  Base = -> ShapeString002
  Dir = (0,0,1)
  DirMode = 0
  FaceMakerClass = Part::FaceMakerBullseye
  FaceMakerMode = 3
  LengthFwd = 0.5
  LengthRev = 0
  Solid = false
  Symmetric = false
